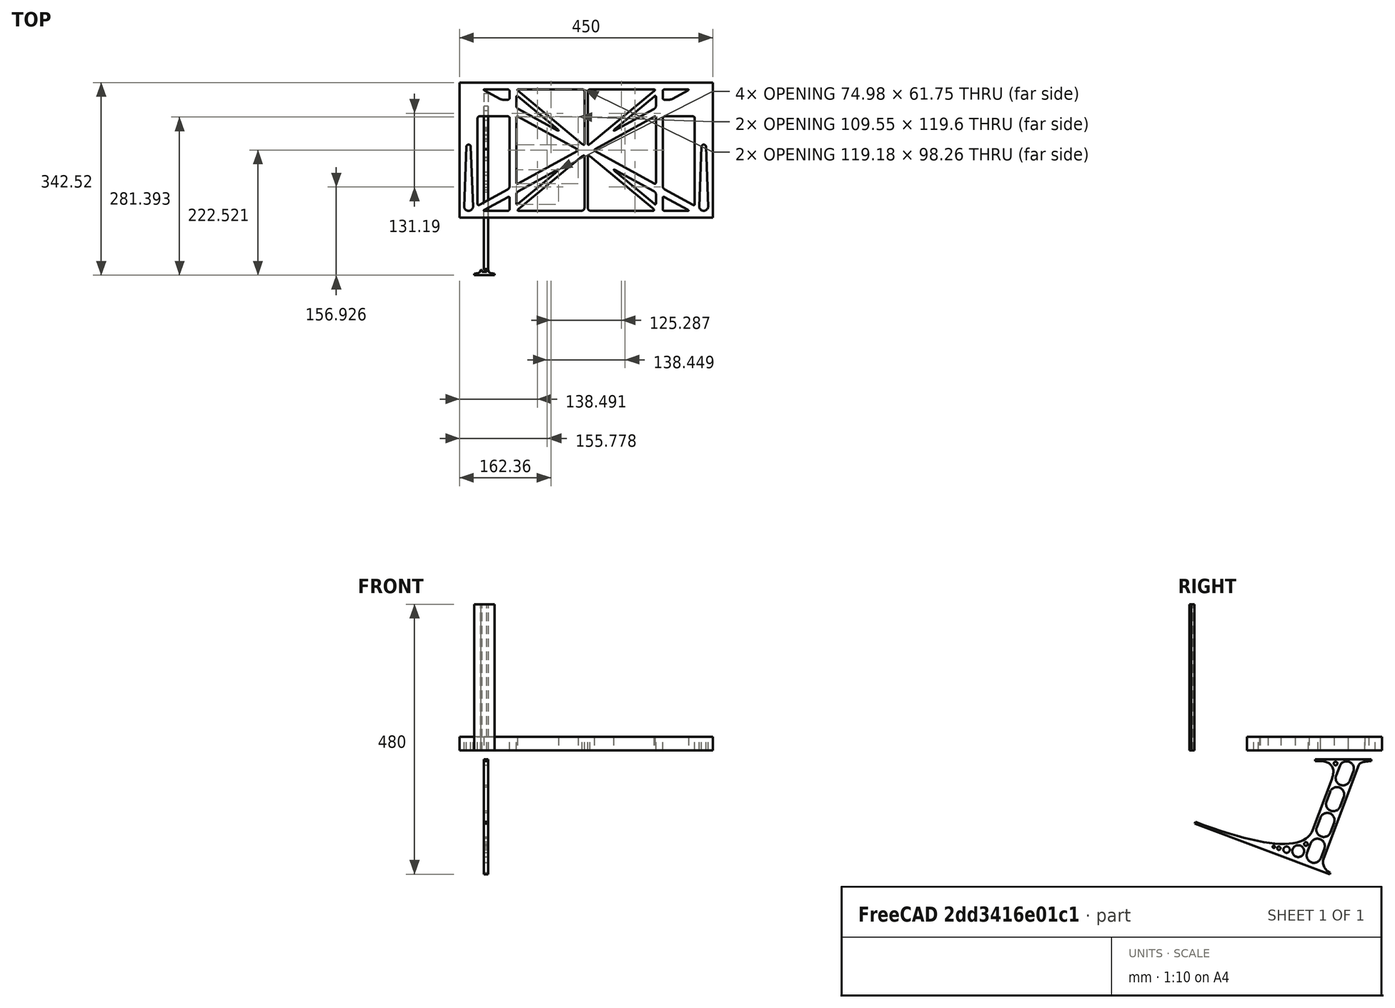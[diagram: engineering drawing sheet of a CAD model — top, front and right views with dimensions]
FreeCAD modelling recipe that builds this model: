
FCSTD DOCUMENT  (FreeCAD 0.19R0.19.2)
Label: laptopStand169FCStd
License: All rights reserved
LicenseURL: http://en.wikipedia.org/wiki/All_rights_reserved
objects: Sketcher::SketchObject×4, Part::Extrusion×3
note: 7 computed .brp shape members not serialized (recipe doc carries the construction recipe); baked Part::Feature solids carry a one-line shape summary decoded from their .brp

FEATURE [Sketcher::SketchObject] Sketch
  FullyConstrained = false
  sketch-geometry (349):
    g0: LineSegment StartX=-10.9272 StartY=-82.7794 StartZ=0 EndX=46.0728 EndY=-51.4823 EndZ=0
    g1: LineSegment StartX=-10.9272 StartY=76.4095 StartZ=0 EndX=-10.9272 EndY=-82.7794 EndZ=0
    g2: LineSegment StartX=46.0728 StartY=76.4095 StartZ=0 EndX=46.0728 EndY=-51.4823 EndZ=0
    g3: LineSegment StartX=-42.9272 StartY=136.221 StartZ=0 EndX=-42.9272 EndY=-103.779 EndZ=0
    g4: LineSegment StartX=407.073 StartY=136.221 StartZ=0 EndX=407.073 EndY=-103.779 EndZ=0
    g5: ArcOfCircle CenterX=-26.9272 CenterY=-83.7794 CenterZ=0 NormalX=0 NormalY=0 NormalZ=1 AngleXU=0 Radius=8 StartAngle=3.14159 EndAngle=6.28319
    g6: ArcOfCircle CenterX=391.073 CenterY=22.1087 CenterZ=0 NormalX=0 NormalY=0 NormalZ=1 AngleXU=0 Radius=8 StartAngle=-4.4e-15 EndAngle=3.14159
    g7: LineSegment StartX=399.073 StartY=22.1087 StartZ=0 EndX=399.073 EndY=-83.7794 EndZ=0
    g8: LineSegment StartX=383.073 StartY=22.1087 StartZ=0 EndX=383.073 EndY=-83.7794 EndZ=0
    g9: ArcOfCircle CenterX=391.073 CenterY=-83.7794 CenterZ=0 NormalX=0 NormalY=0 NormalZ=1 AngleXU=0 Radius=8 StartAngle=3.14159 EndAngle=6.28319
    g10: Circle CenterX=175.022 CenterY=27.0628 CenterZ=0 NormalX=0 NormalY=0 NormalZ=1 AngleXU=0 Radius=1
    g11: Circle CenterX=179.022 CenterY=24.8665 CenterZ=0 NormalX=0 NormalY=0 NormalZ=1 AngleXU=0 Radius=1
    g12: Circle CenterX=179.022 CenterY=27.0628 CenterZ=0 NormalX=0 NormalY=0 NormalZ=1 AngleXU=0 Radius=1
    g13: BSplineCurve PolesCount=3 KnotsCount=2 Degree=2 IsPeriodic=0
    g14: GeomPoint X=175.022 Y=27.0628 Z=0
    g15: GeomPoint X=179.022 Y=27.0628 Z=0
    g16: Circle CenterX=189.124 CenterY=27.0628 CenterZ=0 NormalX=0 NormalY=0 NormalZ=1 AngleXU=0 Radius=1
    g17: Circle CenterX=185.124 CenterY=24.8665 CenterZ=0 NormalX=0 NormalY=0 NormalZ=1 AngleXU=0 Radius=1
    g18: Circle CenterX=185.124 CenterY=27.0628 CenterZ=0 NormalX=0 NormalY=0 NormalZ=1 AngleXU=0 Radius=1
    g19: BSplineCurve PolesCount=3 KnotsCount=2 Degree=2 IsPeriodic=0
    g20: GeomPoint X=189.124 Y=27.0628 Z=0
    g21: GeomPoint X=185.124 Y=27.0628 Z=0
    g22: Circle CenterX=175.022 CenterY=5.37834 CenterZ=0 NormalX=0 NormalY=0 NormalZ=1 AngleXU=0 Radius=1
    g23: Circle CenterX=179.022 CenterY=7.57463 CenterZ=0 NormalX=0 NormalY=0 NormalZ=1 AngleXU=0 Radius=1
    g24: Circle CenterX=179.022 CenterY=5.34704 CenterZ=0 NormalX=0 NormalY=0 NormalZ=1 AngleXU=0 Radius=1
    g25: BSplineCurve PolesCount=3 KnotsCount=2 Degree=2 IsPeriodic=0
    g26: GeomPoint X=175.022 Y=5.37834 Z=0
    g27: GeomPoint X=179.022 Y=5.34704 Z=0
    g28: Circle CenterX=189.124 CenterY=5.37834 CenterZ=0 NormalX=0 NormalY=0 NormalZ=1 AngleXU=0 Radius=1
    g29: Circle CenterX=185.124 CenterY=7.57463 CenterZ=0 NormalX=0 NormalY=0 NormalZ=1 AngleXU=0 Radius=1
    g30: Circle CenterX=185.124 CenterY=5.34704 CenterZ=0 NormalX=0 NormalY=0 NormalZ=1 AngleXU=0 Radius=1
    g31: BSplineCurve PolesCount=3 KnotsCount=2 Degree=2 IsPeriodic=0
    g32: GeomPoint X=189.124 Y=5.37834 Z=0
    g33: GeomPoint X=185.124 Y=5.34704 Z=0
    g34: Circle CenterX=165.871 CenterY=18.1458 CenterZ=0 NormalX=0 NormalY=0 NormalZ=1 AngleXU=0 Radius=1
    g35: Circle CenterX=169.377 CenterY=16.2206 CenterZ=0 NormalX=0 NormalY=0 NormalZ=1 AngleXU=0 Radius=1
    g36: Circle CenterX=165.871 CenterY=14.2954 CenterZ=0 NormalX=0 NormalY=0 NormalZ=1 AngleXU=0 Radius=1
    g37: BSplineCurve PolesCount=3 KnotsCount=2 Degree=2 IsPeriodic=0
    g38: GeomPoint X=165.871 Y=18.1458 Z=0
    g39: GeomPoint X=165.871 Y=14.2954 Z=0
    g40: Circle CenterX=198.275 CenterY=18.1458 CenterZ=0 NormalX=0 NormalY=0 NormalZ=1 AngleXU=0 Radius=1
    g41: Circle CenterX=194.768 CenterY=16.2206 CenterZ=0 NormalX=0 NormalY=0 NormalZ=1 AngleXU=0 Radius=1
    g42: Circle CenterX=198.275 CenterY=14.2954 CenterZ=0 NormalX=0 NormalY=0 NormalZ=1 AngleXU=0 Radius=1
    g43: BSplineCurve PolesCount=3 KnotsCount=2 Degree=2 IsPeriodic=0
    g44: GeomPoint X=198.275 Y=18.1458 Z=0
    g45: GeomPoint X=198.275 Y=14.2954 Z=0
    g46: LineSegment StartX=407.073 StartY=-103.779 StartZ=0 EndX=-42.9272 EndY=-103.779 EndZ=0
    g47: LineSegment StartX=407.073 StartY=136.221 StartZ=0 EndX=-42.9272 EndY=136.221 EndZ=0
    g48: LineSegment StartX=46.0728 StartY=76.4095 StartZ=0 EndX=-10.9272 EndY=76.4095 EndZ=0
    g49: Circle CenterX=125.607 CenterY=54.1951 CenterZ=0 NormalX=0 NormalY=0 NormalZ=1 AngleXU=0 Radius=1
    g50: Circle CenterX=139.632 CenterY=46.4944 CenterZ=0 NormalX=0 NormalY=0 NormalZ=1 AngleXU=0 Radius=1
    g51: Circle CenterX=127.326 CenterY=56.7187 CenterZ=0 NormalX=0 NormalY=0 NormalZ=1 AngleXU=0 Radius=1
    g52: BSplineCurve PolesCount=3 KnotsCount=2 Degree=2 IsPeriodic=0
    g53: GeomPoint X=125.607 Y=54.1951 Z=0
    g54: GeomPoint X=127.326 Y=56.7187 Z=0
    g55: Circle CenterX=236.821 CenterY=56.7187 CenterZ=0 NormalX=0 NormalY=0 NormalZ=1 AngleXU=0 Radius=1
    g56: Circle CenterX=224.513 CenterY=46.4944 CenterZ=0 NormalX=0 NormalY=0 NormalZ=1 AngleXU=0 Radius=1
    g57: Circle CenterX=238.538 CenterY=54.1951 CenterZ=0 NormalX=0 NormalY=0 NormalZ=1 AngleXU=0 Radius=1
    g58: BSplineCurve PolesCount=3 KnotsCount=2 Degree=2 IsPeriodic=0
    g59: GeomPoint X=236.821 Y=56.7187 Z=0
    g60: GeomPoint X=238.538 Y=54.1951 Z=0
    g61: Circle CenterX=238.538 CenterY=-21.7539 CenterZ=0 NormalX=0 NormalY=0 NormalZ=1 AngleXU=0 Radius=1
    g62: Circle CenterX=224.513 CenterY=-14.0532 CenterZ=0 NormalX=0 NormalY=0 NormalZ=1 AngleXU=0 Radius=1
    g63: Circle CenterX=236.821 CenterY=-24.2775 CenterZ=0 NormalX=0 NormalY=0 NormalZ=1 AngleXU=0 Radius=1
    g64: BSplineCurve PolesCount=3 KnotsCount=2 Degree=2 IsPeriodic=0
    g65: GeomPoint X=238.538 Y=-21.7539 Z=0
    g66: GeomPoint X=236.821 Y=-24.2775 Z=0
    g67: Circle CenterX=125.607 CenterY=-21.7539 CenterZ=0 NormalX=0 NormalY=0 NormalZ=1 AngleXU=0 Radius=1
    g68: Circle CenterX=139.632 CenterY=-14.0532 CenterZ=0 NormalX=0 NormalY=0 NormalZ=1 AngleXU=0 Radius=1
    g69: Circle CenterX=127.325 CenterY=-24.2775 CenterZ=0 NormalX=0 NormalY=0 NormalZ=1 AngleXU=0 Radius=1
    g70: BSplineCurve PolesCount=3 KnotsCount=2 Degree=2 IsPeriodic=0
    g71: GeomPoint X=125.607 Y=-21.7539 Z=0
    g72: GeomPoint X=127.325 Y=-24.2775 Z=0
    g73: Circle CenterX=302.996 CenterY=111.695 CenterZ=0 NormalX=0 NormalY=0 NormalZ=1 AngleXU=0 Radius=1
    g74: Circle CenterX=306.073 CenterY=114.251 CenterZ=0 NormalX=0 NormalY=0 NormalZ=1 AngleXU=0 Radius=1
    g75: Circle CenterX=306.073 CenterY=110.251 CenterZ=0 NormalX=0 NormalY=0 NormalZ=1 AngleXU=0 Radius=1
    g76: BSplineCurve PolesCount=3 KnotsCount=2 Degree=2 IsPeriodic=0
    g77: GeomPoint X=302.996 Y=111.695 Z=0
    g78: GeomPoint X=306.073 Y=110.251 Z=0
    g79: Circle CenterX=306.073 CenterY=95.2763 CenterZ=0 NormalX=0 NormalY=0 NormalZ=1 AngleXU=0 Radius=1
    g80: Circle CenterX=306.073 CenterY=91.2763 CenterZ=0 NormalX=0 NormalY=0 NormalZ=1 AngleXU=0 Radius=1
    g81: Circle CenterX=302.567 CenterY=89.3511 CenterZ=0 NormalX=0 NormalY=0 NormalZ=1 AngleXU=0 Radius=1
    g82: BSplineCurve PolesCount=3 KnotsCount=2 Degree=2 IsPeriodic=0
    g83: GeomPoint X=306.073 Y=95.2763 Z=0
    g84: GeomPoint X=302.567 Y=89.3511 Z=0
    g85: LineSegment StartX=306.073 StartY=110.251 StartZ=0 EndX=306.073 EndY=95.2763 EndZ=0
    g86: LineSegment StartX=302.996 StartY=111.695 StartZ=0 EndX=236.821 EndY=56.7187 EndZ=0
    g87: LineSegment StartX=238.538 StartY=54.1951 StartZ=0 EndX=302.567 EndY=89.3511 EndZ=0
    g88: Circle CenterX=61.1496 CenterY=111.695 CenterZ=0 NormalX=0 NormalY=0 NormalZ=1 AngleXU=0 Radius=1
    g89: Circle CenterX=58.0728 CenterY=114.251 CenterZ=0 NormalX=0 NormalY=0 NormalZ=1 AngleXU=0 Radius=1
    g90: Circle CenterX=58.0728 CenterY=110.251 CenterZ=0 NormalX=0 NormalY=0 NormalZ=1 AngleXU=0 Radius=1
    g91: BSplineCurve PolesCount=3 KnotsCount=2 Degree=2 IsPeriodic=0
    g92: GeomPoint X=61.1496 Y=111.695 Z=0
    g93: GeomPoint X=58.0728 Y=110.251 Z=0
    g94: Circle CenterX=61.5791 CenterY=89.3511 CenterZ=0 NormalX=0 NormalY=0 NormalZ=1 AngleXU=0 Radius=1
    g95: Circle CenterX=58.0728 CenterY=91.2763 CenterZ=0 NormalX=0 NormalY=0 NormalZ=1 AngleXU=0 Radius=1
    g96: Circle CenterX=58.0728 CenterY=95.2763 CenterZ=0 NormalX=0 NormalY=0 NormalZ=1 AngleXU=0 Radius=1
    g97: BSplineCurve PolesCount=3 KnotsCount=2 Degree=2 IsPeriodic=0
    g98: GeomPoint X=61.5791 Y=89.3511 Z=0
    g99: GeomPoint X=58.0728 Y=95.2763 Z=0
    g100: LineSegment StartX=58.0728 StartY=110.251 StartZ=0 EndX=58.0728 EndY=95.2763 EndZ=0
    g101: LineSegment StartX=61.1496 StartY=111.695 StartZ=0 EndX=127.326 EndY=56.7187 EndZ=0
    g102: LineSegment StartX=125.607 StartY=54.1951 StartZ=0 EndX=61.5791 EndY=89.3511 EndZ=0
    g103: Circle CenterX=61.5791 CenterY=-56.9099 CenterZ=0 NormalX=0 NormalY=0 NormalZ=1 AngleXU=0 Radius=1
    g104: Circle CenterX=58.0728 CenterY=-58.8351 CenterZ=0 NormalX=0 NormalY=0 NormalZ=1 AngleXU=0 Radius=1
    g105: Circle CenterX=58.0728 CenterY=-62.8351 CenterZ=0 NormalX=0 NormalY=0 NormalZ=1 AngleXU=0 Radius=1
    g106: BSplineCurve PolesCount=3 KnotsCount=2 Degree=2 IsPeriodic=0
    g107: GeomPoint X=61.5791 Y=-56.9099 Z=0
    g108: GeomPoint X=58.0728 Y=-62.8351 Z=0
    g109: Circle CenterX=58.0728 CenterY=-77.8102 CenterZ=0 NormalX=0 NormalY=0 NormalZ=1 AngleXU=0 Radius=1
    g110: Circle CenterX=58.0728 CenterY=-81.8102 CenterZ=0 NormalX=0 NormalY=0 NormalZ=1 AngleXU=0 Radius=1
    g111: Circle CenterX=61.1496 CenterY=-79.2541 CenterZ=0 NormalX=0 NormalY=0 NormalZ=1 AngleXU=0 Radius=1
    g112: BSplineCurve PolesCount=3 KnotsCount=2 Degree=2 IsPeriodic=0
    g113: GeomPoint X=58.0728 Y=-77.8102 Z=0
    g114: GeomPoint X=61.1496 Y=-79.2541 Z=0
    g115: LineSegment StartX=58.0728 StartY=-62.8351 StartZ=0 EndX=58.0728 EndY=-77.8102 EndZ=0
    g116: LineSegment StartX=61.1496 StartY=-79.2541 StartZ=0 EndX=127.325 EndY=-24.2775 EndZ=0
    g117: LineSegment StartX=125.607 StartY=-21.7539 StartZ=0 EndX=61.5791 EndY=-56.9099 EndZ=0
    g118: Circle CenterX=302.567 CenterY=-56.9099 CenterZ=0 NormalX=0 NormalY=0 NormalZ=1 AngleXU=0 Radius=1
    g119: Circle CenterX=306.073 CenterY=-58.8351 CenterZ=0 NormalX=0 NormalY=0 NormalZ=1 AngleXU=0 Radius=1
    g120: Circle CenterX=306.073 CenterY=-62.8351 CenterZ=0 NormalX=0 NormalY=0 NormalZ=1 AngleXU=0 Radius=1
    g121: BSplineCurve PolesCount=3 KnotsCount=2 Degree=2 IsPeriodic=0
    g122: GeomPoint X=302.567 Y=-56.9099 Z=0
    g123: GeomPoint X=306.073 Y=-62.8351 Z=0
    g124: Circle CenterX=302.996 CenterY=-79.2541 CenterZ=0 NormalX=0 NormalY=0 NormalZ=1 AngleXU=0 Radius=1
    g125: Circle CenterX=306.073 CenterY=-81.8102 CenterZ=0 NormalX=0 NormalY=0 NormalZ=1 AngleXU=0 Radius=1
    g126: Circle CenterX=306.073 CenterY=-77.8102 CenterZ=0 NormalX=0 NormalY=0 NormalZ=1 AngleXU=0 Radius=1
    g127: BSplineCurve PolesCount=3 KnotsCount=2 Degree=2 IsPeriodic=0
    g128: GeomPoint X=302.996 Y=-79.2541 Z=0
    g129: GeomPoint X=306.073 Y=-77.8102 Z=0
    g130: LineSegment StartX=306.073 StartY=-62.8351 StartZ=0 EndX=306.073 EndY=-77.8102 EndZ=0
    g131: LineSegment StartX=302.996 StartY=-79.2541 StartZ=0 EndX=236.821 EndY=-24.2775 EndZ=0
    g132: LineSegment StartX=238.538 StartY=-21.7539 StartZ=0 EndX=302.567 EndY=-56.9099 EndZ=0
    g133: Circle CenterX=61.6457 CenterY=-88.8112 CenterZ=0 NormalX=0 NormalY=0 NormalZ=1 AngleXU=0 Radius=1
    g134: Circle CenterX=58.0728 CenterY=-91.7794 CenterZ=0 NormalX=0 NormalY=0 NormalZ=1 AngleXU=0 Radius=1
    g135: Circle CenterX=63.9135 CenterY=-91.7794 CenterZ=0 NormalX=0 NormalY=0 NormalZ=1 AngleXU=0 Radius=1
    g136: BSplineCurve PolesCount=3 KnotsCount=2 Degree=2 IsPeriodic=0
    g137: GeomPoint X=61.6457 Y=-88.8112 Z=0
    g138: GeomPoint X=63.9135 Y=-91.7794 Z=0
    g139: Circle CenterX=179.022 CenterY=-85.8163 CenterZ=0 NormalX=0 NormalY=0 NormalZ=1 AngleXU=0 Radius=1
    g140: Circle CenterX=179.022 CenterY=-91.7794 CenterZ=0 NormalX=0 NormalY=0 NormalZ=1 AngleXU=0 Radius=1
    g141: Circle CenterX=171.895 CenterY=-91.7794 CenterZ=0 NormalX=0 NormalY=0 NormalZ=1 AngleXU=0 Radius=1
    g142: BSplineCurve PolesCount=3 KnotsCount=2 Degree=2 IsPeriodic=0
    g143: GeomPoint X=179.022 Y=-85.8163 Z=0
    g144: GeomPoint X=171.895 Y=-91.7794 Z=0
    g145: Circle CenterX=185.124 CenterY=-86.2028 CenterZ=0 NormalX=0 NormalY=0 NormalZ=1 AngleXU=0 Radius=1
    g146: Circle CenterX=185.124 CenterY=-91.7794 CenterZ=0 NormalX=0 NormalY=0 NormalZ=1 AngleXU=0 Radius=1
    g147: Circle CenterX=191.747 CenterY=-91.7794 CenterZ=0 NormalX=0 NormalY=0 NormalZ=1 AngleXU=0 Radius=1
    g148: BSplineCurve PolesCount=3 KnotsCount=2 Degree=2 IsPeriodic=0
    g149: GeomPoint X=185.124 Y=-86.2028 Z=0
    g150: GeomPoint X=191.747 Y=-91.7794 Z=0
    g151: Circle CenterX=299.888 CenterY=-86.6413 CenterZ=0 NormalX=0 NormalY=0 NormalZ=1 AngleXU=0 Radius=1
    g152: Circle CenterX=306.073 CenterY=-91.7794 CenterZ=0 NormalX=0 NormalY=0 NormalZ=1 AngleXU=0 Radius=1
    g153: Circle CenterX=298.776 CenterY=-91.7794 CenterZ=0 NormalX=0 NormalY=0 NormalZ=1 AngleXU=0 Radius=1
    g154: BSplineCurve PolesCount=3 KnotsCount=2 Degree=2 IsPeriodic=0
    g155: GeomPoint X=299.888 Y=-86.6413 Z=0
    g156: GeomPoint X=298.776 Y=-91.7794 Z=0
    g157: LineSegment StartX=189.124 StartY=5.37834 StartZ=0 EndX=299.888 EndY=-86.6413 EndZ=0
    g158: LineSegment StartX=298.776 StartY=-91.7794 StartZ=0 EndX=191.747 EndY=-91.7794 EndZ=0
    g159: LineSegment StartX=185.124 StartY=-86.2028 StartZ=0 EndX=185.124 EndY=5.34704 EndZ=0
    g160: LineSegment StartX=179.022 StartY=5.34704 StartZ=0 EndX=179.022 EndY=-85.8163 EndZ=0
    g161: LineSegment StartX=171.895 StartY=-91.7794 StartZ=0 EndX=63.9135 EndY=-91.7794 EndZ=0
    g162: LineSegment StartX=61.6457 StartY=-88.8112 StartZ=0 EndX=175.022 EndY=5.37834 EndZ=0
    g163: Circle CenterX=302.073 CenterY=124.221 CenterZ=0 NormalX=0 NormalY=0 NormalZ=1 AngleXU=0 Radius=1
    g164: Circle CenterX=306.073 CenterY=124.221 CenterZ=0 NormalX=0 NormalY=0 NormalZ=1 AngleXU=0 Radius=1
    g165: Circle CenterX=302.996 CenterY=121.665 CenterZ=0 NormalX=0 NormalY=0 NormalZ=1 AngleXU=0 Radius=1
    g166: BSplineCurve PolesCount=3 KnotsCount=2 Degree=2 IsPeriodic=0
    g167: GeomPoint X=302.073 Y=124.221 Z=0
    g168: GeomPoint X=302.996 Y=121.665 Z=0
    g169: Circle CenterX=189.124 CenterY=124.221 CenterZ=0 NormalX=0 NormalY=0 NormalZ=1 AngleXU=0 Radius=1
    g170: Circle CenterX=185.124 CenterY=124.221 CenterZ=0 NormalX=0 NormalY=0 NormalZ=1 AngleXU=0 Radius=1
    g171: Circle CenterX=185.124 CenterY=120.221 CenterZ=0 NormalX=0 NormalY=0 NormalZ=1 AngleXU=0 Radius=1
    g172: BSplineCurve PolesCount=3 KnotsCount=2 Degree=2 IsPeriodic=0
    g173: GeomPoint X=189.124 Y=124.221 Z=0
    g174: GeomPoint X=185.124 Y=120.221 Z=0
    g175: Circle CenterX=175.022 CenterY=124.221 CenterZ=0 NormalX=0 NormalY=0 NormalZ=1 AngleXU=0 Radius=1
    g176: Circle CenterX=179.022 CenterY=124.221 CenterZ=0 NormalX=0 NormalY=0 NormalZ=1 AngleXU=0 Radius=1
    g177: Circle CenterX=179.022 CenterY=120.221 CenterZ=0 NormalX=0 NormalY=0 NormalZ=1 AngleXU=0 Radius=1
    g178: BSplineCurve PolesCount=3 KnotsCount=2 Degree=2 IsPeriodic=0
    g179: GeomPoint X=175.022 Y=124.221 Z=0
    g180: GeomPoint X=179.022 Y=120.221 Z=0
    g181: Circle CenterX=62.0728 CenterY=124.221 CenterZ=0 NormalX=0 NormalY=0 NormalZ=1 AngleXU=0 Radius=1
    g182: Circle CenterX=58.0728 CenterY=124.221 CenterZ=0 NormalX=0 NormalY=0 NormalZ=1 AngleXU=0 Radius=1
    g183: Circle CenterX=61.1496 CenterY=121.665 CenterZ=0 NormalX=0 NormalY=0 NormalZ=1 AngleXU=0 Radius=1
    g184: BSplineCurve PolesCount=3 KnotsCount=2 Degree=2 IsPeriodic=0
    g185: GeomPoint X=62.0728 Y=124.221 Z=0
    g186: GeomPoint X=61.1496 Y=121.665 Z=0
    g187: LineSegment StartX=62.0728 StartY=124.221 StartZ=0 EndX=175.022 EndY=124.221 EndZ=0
    g188: LineSegment StartX=179.022 StartY=120.221 StartZ=0 EndX=179.022 EndY=27.0628 EndZ=0
    g189: LineSegment StartX=185.124 StartY=27.0628 StartZ=0 EndX=185.124 EndY=120.221 EndZ=0
    g190: LineSegment StartX=189.124 StartY=124.221 StartZ=0 EndX=302.073 EndY=124.221 EndZ=0
    g191: LineSegment StartX=302.996 StartY=121.665 StartZ=0 EndX=189.124 EndY=27.0628 EndZ=0
    g192: LineSegment StartX=175.022 StartY=27.0628 StartZ=0 EndX=61.1496 EndY=121.665 EndZ=0
    g193: Circle CenterX=61.5791 CenterY=75.4095 CenterZ=0 NormalX=0 NormalY=0 NormalZ=1 AngleXU=0 Radius=1
    g194: Circle CenterX=58.0728 CenterY=77.3346 CenterZ=0 NormalX=0 NormalY=0 NormalZ=1 AngleXU=0 Radius=1
    g195: Circle CenterX=58.0728 CenterY=73.3346 CenterZ=0 NormalX=0 NormalY=0 NormalZ=1 AngleXU=0 Radius=1
    g196: BSplineCurve PolesCount=3 KnotsCount=2 Degree=2 IsPeriodic=0
    g197: GeomPoint X=61.5791 Y=75.4095 Z=0
    g198: GeomPoint X=58.0728 Y=73.3346 Z=0
    g199: Circle CenterX=58.0728 CenterY=-40.8935 CenterZ=0 NormalX=0 NormalY=0 NormalZ=1 AngleXU=0 Radius=1
    g200: Circle CenterX=58.0728 CenterY=-44.8935 CenterZ=0 NormalX=0 NormalY=0 NormalZ=1 AngleXU=0 Radius=1
    g201: Circle CenterX=61.5791 CenterY=-42.9683 CenterZ=0 NormalX=0 NormalY=0 NormalZ=1 AngleXU=0 Radius=1
    g202: BSplineCurve PolesCount=3 KnotsCount=2 Degree=2 IsPeriodic=0
    g203: GeomPoint X=58.0728 Y=-40.8935 Z=0
    g204: GeomPoint X=61.5791 Y=-42.9683 Z=0
    g205: LineSegment StartX=61.5791 StartY=-42.9683 StartZ=0 EndX=165.871 EndY=14.2954 EndZ=0
    g206: LineSegment StartX=165.871 StartY=18.1458 StartZ=0 EndX=61.5791 EndY=75.4095 EndZ=0
    g207: LineSegment StartX=58.0728 StartY=73.3346 StartZ=0 EndX=58.0728 EndY=-40.8935 EndZ=0
    g208: Circle CenterX=302.567 CenterY=-42.9683 CenterZ=0 NormalX=0 NormalY=0 NormalZ=1 AngleXU=0 Radius=1
    g209: Circle CenterX=306.073 CenterY=-44.8935 CenterZ=0 NormalX=0 NormalY=0 NormalZ=1 AngleXU=0 Radius=1
    g210: Circle CenterX=306.073 CenterY=-40.8935 CenterZ=0 NormalX=0 NormalY=0 NormalZ=1 AngleXU=0 Radius=1
    g211: BSplineCurve PolesCount=3 KnotsCount=2 Degree=2 IsPeriodic=0
    g212: GeomPoint X=302.567 Y=-42.9683 Z=0
    g213: GeomPoint X=306.073 Y=-40.8935 Z=0
    g214: Circle CenterX=306.073 CenterY=73.3346 CenterZ=0 NormalX=0 NormalY=0 NormalZ=1 AngleXU=0 Radius=1
    g215: Circle CenterX=306.073 CenterY=77.3346 CenterZ=0 NormalX=0 NormalY=0 NormalZ=1 AngleXU=0 Radius=1
    g216: Circle CenterX=302.567 CenterY=75.4095 CenterZ=0 NormalX=0 NormalY=0 NormalZ=1 AngleXU=0 Radius=1
    g217: BSplineCurve PolesCount=3 KnotsCount=2 Degree=2 IsPeriodic=0
    g218: GeomPoint X=306.073 Y=73.3346 Z=0
    g219: GeomPoint X=302.567 Y=75.4095 Z=0
    g220: LineSegment StartX=302.567 StartY=-42.9683 StartZ=0 EndX=198.275 EndY=14.2954 EndZ=0
    g221: LineSegment StartX=198.275 StartY=18.1458 StartZ=0 EndX=302.567 EndY=75.4095 EndZ=0
    g222: LineSegment StartX=306.073 StartY=73.3346 StartZ=0 EndX=306.073 EndY=-40.8935 EndZ=0
    g223: LineSegment StartX=322.073 StartY=105.865 StartZ=0 EndX=328.643 EndY=105.865 EndZ=0
    g224: LineSegment StartX=318.073 StartY=120.221 StartZ=0 EndX=318.073 EndY=109.865 EndZ=0
    g225: LineSegment StartX=336.157 StartY=107.779 StartZ=0 EndX=362.567 EndY=122.294 EndZ=0
    g226: Circle CenterX=362.073 CenterY=124.221 CenterZ=0 NormalX=0 NormalY=0 NormalZ=1 AngleXU=0 Radius=1
    g227: Circle CenterX=366.073 CenterY=124.221 CenterZ=0 NormalX=0 NormalY=0 NormalZ=1 AngleXU=0 Radius=1
    g228: Circle CenterX=362.567 CenterY=122.294 CenterZ=0 NormalX=0 NormalY=0 NormalZ=1 AngleXU=0 Radius=1
    g229: BSplineCurve PolesCount=3 KnotsCount=2 Degree=2 IsPeriodic=0
    g230: GeomPoint X=362.073 Y=124.221 Z=0
    g231: GeomPoint X=362.567 Y=122.294 Z=0
    g232: Circle CenterX=322.073 CenterY=124.221 CenterZ=0 NormalX=0 NormalY=0 NormalZ=1 AngleXU=0 Radius=1
    g233: Circle CenterX=318.073 CenterY=124.221 CenterZ=0 NormalX=0 NormalY=0 NormalZ=1 AngleXU=0 Radius=1
    g234: Circle CenterX=318.073 CenterY=120.221 CenterZ=0 NormalX=0 NormalY=0 NormalZ=1 AngleXU=0 Radius=1
    g235: BSplineCurve PolesCount=3 KnotsCount=2 Degree=2 IsPeriodic=0
    g236: GeomPoint X=322.073 Y=124.221 Z=0
    g237: GeomPoint X=318.073 Y=120.221 Z=0
    g238: Circle CenterX=322.073 CenterY=105.865 CenterZ=0 NormalX=0 NormalY=0 NormalZ=1 AngleXU=0 Radius=1
    g239: Circle CenterX=318.073 CenterY=105.865 CenterZ=0 NormalX=0 NormalY=0 NormalZ=1 AngleXU=0 Radius=1
    g240: Circle CenterX=318.073 CenterY=109.865 CenterZ=0 NormalX=0 NormalY=0 NormalZ=1 AngleXU=0 Radius=1
    g241: BSplineCurve PolesCount=3 KnotsCount=2 Degree=2 IsPeriodic=0
    g242: GeomPoint X=322.073 Y=105.865 Z=0
    g243: GeomPoint X=318.073 Y=109.865 Z=0
    g244: Circle CenterX=336.157 CenterY=107.779 CenterZ=0 NormalX=0 NormalY=0 NormalZ=1 AngleXU=0 Radius=1
    g245: Circle CenterX=332.651 CenterY=105.853 CenterZ=0 NormalX=0 NormalY=0 NormalZ=1 AngleXU=0 Radius=1
    g246: Circle CenterX=328.643 CenterY=105.865 CenterZ=0 NormalX=0 NormalY=0 NormalZ=1 AngleXU=0 Radius=1
    g247: BSplineCurve PolesCount=3 KnotsCount=2 Degree=2 IsPeriodic=0
    g248: GeomPoint X=336.157 Y=107.779 Z=0
    g249: GeomPoint X=328.643 Y=105.865 Z=0
    g250: LineSegment StartX=322.073 StartY=124.221 StartZ=0 EndX=362.073 EndY=124.221 EndZ=0
    g251: Circle CenterX=371.567 CenterY=-80.8644 CenterZ=0 NormalX=0 NormalY=0 NormalZ=1 AngleXU=0 Radius=1
    g252: Circle CenterX=375.073 CenterY=-82.7896 CenterZ=0 NormalX=0 NormalY=0 NormalZ=1 AngleXU=0 Radius=1
    g253: Circle CenterX=375.073 CenterY=-78.7896 CenterZ=0 NormalX=0 NormalY=0 NormalZ=1 AngleXU=0 Radius=1
    g254: BSplineCurve PolesCount=3 KnotsCount=2 Degree=2 IsPeriodic=0
    g255: GeomPoint X=371.567 Y=-80.8644 Z=0
    g256: GeomPoint X=375.073 Y=-78.7896 Z=0
    g257: Circle CenterX=321.579 CenterY=-53.4075 CenterZ=0 NormalX=0 NormalY=0 NormalZ=1 AngleXU=0 Radius=1
    g258: Circle CenterX=318.073 CenterY=-51.4823 CenterZ=0 NormalX=0 NormalY=0 NormalZ=1 AngleXU=0 Radius=1
    g259: Circle CenterX=318.073 CenterY=-47.4805 CenterZ=0 NormalX=0 NormalY=0 NormalZ=1 AngleXU=0 Radius=1
    g260: BSplineCurve PolesCount=3 KnotsCount=2 Degree=2 IsPeriodic=0
    g261: GeomPoint X=321.579 Y=-53.4075 Z=0
    g262: GeomPoint X=318.073 Y=-47.4805 Z=0
    g263: LineSegment StartX=371.567 StartY=-80.8644 StartZ=0 EndX=321.579 EndY=-53.4075 EndZ=0
    g264: Circle CenterX=321.579 CenterY=-67.3492 CenterZ=0 NormalX=0 NormalY=0 NormalZ=1 AngleXU=0 Radius=1
    g265: Circle CenterX=318.073 CenterY=-65.424 CenterZ=0 NormalX=0 NormalY=0 NormalZ=1 AngleXU=0 Radius=1
    g266: Circle CenterX=318.073 CenterY=-69.424 CenterZ=0 NormalX=0 NormalY=0 NormalZ=1 AngleXU=0 Radius=1
    g267: BSplineCurve PolesCount=3 KnotsCount=2 Degree=2 IsPeriodic=0
    g268: GeomPoint X=321.579 Y=-67.3492 Z=0
    g269: GeomPoint X=318.073 Y=-69.424 Z=0
    g270: Circle CenterX=362.567 CenterY=-89.8542 CenterZ=0 NormalX=0 NormalY=0 NormalZ=1 AngleXU=0 Radius=1
    g271: Circle CenterX=366.073 CenterY=-91.7794 CenterZ=0 NormalX=0 NormalY=0 NormalZ=1 AngleXU=0 Radius=1
    g272: Circle CenterX=362.073 CenterY=-91.7794 CenterZ=0 NormalX=0 NormalY=0 NormalZ=1 AngleXU=0 Radius=1
    g273: BSplineCurve PolesCount=3 KnotsCount=2 Degree=2 IsPeriodic=0
    g274: GeomPoint X=362.567 Y=-89.8542 Z=0
    g275: GeomPoint X=362.073 Y=-91.7794 Z=0
    g276: Circle CenterX=322.073 CenterY=-91.7794 CenterZ=0 NormalX=0 NormalY=0 NormalZ=1 AngleXU=0 Radius=1
    g277: Circle CenterX=318.073 CenterY=-91.7794 CenterZ=0 NormalX=0 NormalY=0 NormalZ=1 AngleXU=0 Radius=1
    g278: Circle CenterX=318.073 CenterY=-87.7794 CenterZ=0 NormalX=0 NormalY=0 NormalZ=1 AngleXU=0 Radius=1
    g279: BSplineCurve PolesCount=3 KnotsCount=2 Degree=2 IsPeriodic=0
    g280: GeomPoint X=322.073 Y=-91.7794 Z=0
    g281: GeomPoint X=318.073 Y=-87.7794 Z=0
    g282: LineSegment StartX=362.567 StartY=-89.8542 StartZ=0 EndX=321.579 EndY=-67.3492 EndZ=0
    g283: LineSegment StartX=318.073 StartY=-69.424 StartZ=0 EndX=318.073 EndY=-87.7794 EndZ=0
    g284: LineSegment StartX=322.073 StartY=-91.7794 StartZ=0 EndX=362.073 EndY=-91.7794 EndZ=0
    g285: Circle CenterX=2.07281 CenterY=124.221 CenterZ=0 NormalX=0 NormalY=0 NormalZ=1 AngleXU=0 Radius=1
    g286: Circle CenterX=1.57905 CenterY=122.295 CenterZ=0 NormalX=0 NormalY=0 NormalZ=1 AngleXU=0 Radius=1
    g287: BSplineCurve PolesCount=3 KnotsCount=2 Degree=2 IsPeriodic=0
    g288: GeomPoint X=2.07281 Y=124.221 Z=0
    g289: GeomPoint X=1.57905 Y=122.295 Z=0
    g290: Circle CenterX=42.0728 CenterY=124.221 CenterZ=0 NormalX=0 NormalY=0 NormalZ=1 AngleXU=0 Radius=1
    g291: Circle CenterX=46.0728 CenterY=124.221 CenterZ=0 NormalX=0 NormalY=0 NormalZ=1 AngleXU=0 Radius=1
    g292: Circle CenterX=46.0728 CenterY=120.221 CenterZ=0 NormalX=0 NormalY=0 NormalZ=1 AngleXU=0 Radius=1
    g293: BSplineCurve PolesCount=3 KnotsCount=2 Degree=2 IsPeriodic=0
    g294: GeomPoint X=42.0728 Y=124.221 Z=0
    g295: GeomPoint X=46.0728 Y=120.221 Z=0
    g296: Circle CenterX=46.0728 CenterY=109.865 CenterZ=0 NormalX=0 NormalY=0 NormalZ=1 AngleXU=0 Radius=1
    g297: Circle CenterX=46.0728 CenterY=105.865 CenterZ=0 NormalX=0 NormalY=0 NormalZ=1 AngleXU=0 Radius=1
    g298: Circle CenterX=42.0728 CenterY=105.865 CenterZ=0 NormalX=0 NormalY=0 NormalZ=1 AngleXU=0 Radius=1
    g299: BSplineCurve PolesCount=3 KnotsCount=2 Degree=2 IsPeriodic=0
    g300: GeomPoint X=46.0728 Y=109.865 Z=0
    g301: GeomPoint X=42.0728 Y=105.865 Z=0
    g302: Circle CenterX=35.5028 CenterY=105.865 CenterZ=0 NormalX=0 NormalY=0 NormalZ=1 AngleXU=0 Radius=1
    g303: Circle CenterX=31.5028 CenterY=105.865 CenterZ=0 NormalX=0 NormalY=0 NormalZ=1 AngleXU=0 Radius=1
    g304: Circle CenterX=27.9965 CenterY=107.79 CenterZ=0 NormalX=0 NormalY=0 NormalZ=1 AngleXU=0 Radius=1
    g305: BSplineCurve PolesCount=3 KnotsCount=2 Degree=2 IsPeriodic=0
    g306: GeomPoint X=35.5028 Y=105.865 Z=0
    g307: GeomPoint X=27.9965 Y=107.79 Z=0
    g308: LineSegment StartX=2.07281 StartY=124.221 StartZ=0 EndX=42.0728 EndY=124.221 EndZ=0
    g309: LineSegment StartX=46.0728 StartY=120.221 StartZ=0 EndX=46.0728 EndY=109.865 EndZ=0
    g310: LineSegment StartX=42.0728 StartY=105.865 StartZ=0 EndX=35.5028 EndY=105.865 EndZ=0
    g311: LineSegment StartX=27.9965 StartY=107.79 StartZ=0 EndX=1.57905 EndY=122.295 EndZ=0
    g312: Circle CenterX=42.5666 CenterY=-67.3492 CenterZ=0 NormalX=0 NormalY=0 NormalZ=1 AngleXU=0 Radius=1
    g313: Circle CenterX=46.0728 CenterY=-65.424 CenterZ=0 NormalX=0 NormalY=0 NormalZ=1 AngleXU=0 Radius=1
    g314: Circle CenterX=46.0728 CenterY=-69.424 CenterZ=0 NormalX=0 NormalY=0 NormalZ=1 AngleXU=0 Radius=1
    g315: BSplineCurve PolesCount=3 KnotsCount=2 Degree=2 IsPeriodic=0
    g316: GeomPoint X=42.5666 Y=-67.3492 Z=0
    g317: GeomPoint X=46.0728 Y=-69.424 Z=0
    g318: Circle CenterX=46.0728 CenterY=-87.7794 CenterZ=0 NormalX=0 NormalY=0 NormalZ=1 AngleXU=0 Radius=1
    g319: Circle CenterX=46.0728 CenterY=-91.7794 CenterZ=0 NormalX=0 NormalY=0 NormalZ=1 AngleXU=0 Radius=1
    g320: Circle CenterX=42.0728 CenterY=-91.7794 CenterZ=0 NormalX=0 NormalY=0 NormalZ=1 AngleXU=0 Radius=1
    g321: BSplineCurve PolesCount=3 KnotsCount=2 Degree=2 IsPeriodic=0
    g322: GeomPoint X=46.0728 Y=-87.7794 Z=0
    g323: GeomPoint X=42.0728 Y=-91.7794 Z=0
    g324: Circle CenterX=2.07281 CenterY=-91.7794 CenterZ=0 NormalX=0 NormalY=0 NormalZ=1 AngleXU=0 Radius=1
    g325: Circle CenterX=-1.92719 CenterY=-91.7794 CenterZ=0 NormalX=0 NormalY=0 NormalZ=1 AngleXU=0 Radius=1
    g326: Circle CenterX=1.57905 CenterY=-89.8542 CenterZ=0 NormalX=0 NormalY=0 NormalZ=1 AngleXU=0 Radius=1
    g327: BSplineCurve PolesCount=3 KnotsCount=2 Degree=2 IsPeriodic=0
    g328: GeomPoint X=2.07281 Y=-91.7794 Z=0
    g329: GeomPoint X=1.57905 Y=-89.8542 Z=0
    g330: LineSegment StartX=2.07281 StartY=-91.7794 StartZ=0 EndX=42.0728 EndY=-91.7794 EndZ=0
    g331: LineSegment StartX=46.0728 StartY=-87.7794 StartZ=0 EndX=46.0728 EndY=-69.424 EndZ=0
    g332: LineSegment StartX=42.5666 StartY=-67.3492 StartZ=0 EndX=1.57905 EndY=-89.8542 EndZ=0
    g333: Circle CenterX=322.073 CenterY=76.4095 CenterZ=0 NormalX=0 NormalY=0 NormalZ=1 AngleXU=0 Radius=4
    g334: BSplineCurve PolesCount=3 KnotsCount=2 Degree=2 IsPeriodic=0
    g335: GeomPoint X=318.073 Y=72.4095 Z=0
    g336: GeomPoint X=322.073 Y=76.4095 Z=0
    g337: Circle CenterX=375.073 CenterY=72.4095 CenterZ=0 NormalX=0 NormalY=0 NormalZ=1 AngleXU=0 Radius=1
    g338: Circle CenterX=375.073 CenterY=76.4095 CenterZ=0 NormalX=0 NormalY=0 NormalZ=1 AngleXU=0 Radius=1
    g339: Circle CenterX=371.073 CenterY=76.4095 CenterZ=0 NormalX=0 NormalY=0 NormalZ=1 AngleXU=0 Radius=1
    g340: BSplineCurve PolesCount=3 KnotsCount=2 Degree=2 IsPeriodic=0
    g341: GeomPoint X=375.073 Y=72.4095 Z=0
    g342: GeomPoint X=371.073 Y=76.4095 Z=0
    g343: LineSegment StartX=322.073 StartY=76.4095 StartZ=0 EndX=371.073 EndY=76.4095 EndZ=0
    g344: LineSegment StartX=318.073 StartY=72.4095 StartZ=0 EndX=318.073 EndY=-47.4805 EndZ=0
    g345: LineSegment StartX=375.073 StartY=72.4095 StartZ=0 EndX=375.073 EndY=-78.7896 EndZ=0
    g346: ArcOfCircle CenterX=-26.9272 CenterY=22.1087 CenterZ=0 NormalX=0 NormalY=0 NormalZ=1 AngleXU=0 Radius=4 StartAngle=5e-16 EndAngle=3.14159
    g347: LineSegment StartX=-30.9272 StartY=22.1087 StartZ=0 EndX=-34.9272 EndY=-83.7794 EndZ=0
    g348: LineSegment StartX=-18.9272 StartY=-83.7794 StartZ=0 EndX=-22.9272 EndY=22.1087 EndZ=0
  constraints (572):
    c: Coincident(g0,g2)
    c: Block(g0)
    c: Block(g1)
    c: Vertical(g3)
    c: Vertical(g4)
    c: Block(g4)
    c: Block(g3)
    c: Tangent(g6,g7) = 1.5708
    c: Tangent(g7,g9) = 1.5708
    c: Equal(g6,g9)
    c: Coincident(g8,g6)
    c: Coincident(g8,g9)
    c: Block(g7)
    c: Block(g8)
    c: Weight(g10) = 1
    c: Equal(g10,g11)
    c: Equal(g10,g12)
    c: InternalAlignment(g10,g13)
    c: InternalAlignment(g11,g13)
    c: InternalAlignment(g12,g13)
    c: InternalAlignment(g14,g13)
    c: InternalAlignment(g15,g13)
    c: Weight(g16) = 1
    c: Equal(g16,g17)
    c: Equal(g16,g18)
    c: InternalAlignment(g16,g19)
    c: InternalAlignment(g17,g19)
    c: InternalAlignment(g18,g19)
    c: InternalAlignment(g20,g19)
    c: InternalAlignment(g21,g19)
    c: Block(g19)
    c: Block(g13)
    c: Weight(g22) = 1
    c: Equal(g22,g23)
    c: Equal(g22,g24)
    c: InternalAlignment(g22,g25)
    c: InternalAlignment(g23,g25)
    c: InternalAlignment(g24,g25)
    c: InternalAlignment(g26,g25)
    c: InternalAlignment(g27,g25)
    c: Weight(g28) = 1
    c: Equal(g28,g29)
    c: Equal(g28,g30)
    c: InternalAlignment(g28,g31)
    c: InternalAlignment(g29,g31)
    c: InternalAlignment(g30,g31)
    c: InternalAlignment(g32,g31)
    c: InternalAlignment(g33,g31)
    c: Block(g31)
    c: Block(g25)
    c: Weight(g34) = 1
    c: Equal(g34,g35)
    c: Equal(g34,g36)
    c: InternalAlignment(g34,g37)
    c: InternalAlignment(g35,g37)
    c: InternalAlignment(g36,g37)
    c: InternalAlignment(g38,g37)
    c: InternalAlignment(g39,g37)
    c: Weight(g40) = 1
    c: Equal(g40,g41)
    c: Equal(g40,g42)
    c: InternalAlignment(g40,g43)
    c: InternalAlignment(g41,g43)
    c: InternalAlignment(g42,g43)
    c: InternalAlignment(g44,g43)
    c: InternalAlignment(g45,g43)
    c: Block(g37)
    c: Block(g43)
    c: Coincident(g46,g4)
    c: Coincident(g46,g3)
    c: Horizontal(g46)
    c: Distance(g46) = 450
    c: Coincident(g47,g4)
    c: Coincident(g47,g3)
    c: Horizontal(g47)
    c: Horizontal(g48)
    c: Coincident(g2,g48)
    c: Block(g48)
    c: Coincident(g1,g48)
    c: Weight(g49) = 1
    c: Equal(g49,g50)
    c: Equal(g49,g51)
    c: InternalAlignment(g49,g52)
    c: InternalAlignment(g50,g52)
    c: InternalAlignment(g51,g52)
    c: InternalAlignment(g53,g52)
    c: InternalAlignment(g54,g52)
    c: Block(g52)
    c: Weight(g55) = 1
    c: Equal(g55,g56)
    c: Equal(g55,g57)
    c: InternalAlignment(g55,g58)
    c: InternalAlignment(g56,g58)
    c: InternalAlignment(g57,g58)
    c: InternalAlignment(g59,g58)
    c: InternalAlignment(g60,g58)
    c: Block(g58)
    c: Weight(g61) = 1
    c: Equal(g61,g62)
    c: Equal(g61,g63)
    c: InternalAlignment(g61,g64)
    c: InternalAlignment(g62,g64)
    c: InternalAlignment(g63,g64)
    c: InternalAlignment(g65,g64)
    c: InternalAlignment(g66,g64)
    c: Block(g64)
    c: Weight(g67) = 1
    c: Equal(g67,g68)
    c: Equal(g67,g69)
    c: InternalAlignment(g67,g70)
    c: InternalAlignment(g68,g70)
    c: InternalAlignment(g69,g70)
    c: InternalAlignment(g71,g70)
    c: InternalAlignment(g72,g70)
    c: Block(g70)
    c: Weight(g73) = 1
    c: Equal(g73,g74)
    c: Equal(g73,g75)
    c: InternalAlignment(g73,g76)
    c: InternalAlignment(g74,g76)
    c: InternalAlignment(g75,g76)
    c: InternalAlignment(g77,g76)
    c: InternalAlignment(g78,g76)
    c: Weight(g79) = 1
    c: Equal(g79,g80)
    c: Equal(g79,g81)
    c: InternalAlignment(g79,g82)
    c: InternalAlignment(g80,g82)
    c: InternalAlignment(g81,g82)
    c: InternalAlignment(g83,g82)
    c: InternalAlignment(g84,g82)
    c: Block(g76)
    c: Block(g82)
    c: Coincident(g85,g76)
    c: Coincident(g85,g82)
    c: Vertical(g85)
    c: Coincident(g86,g76)
    c: Coincident(g86,g58)
    c: Coincident(g87,g58)
    c: Coincident(g87,g82)
    c: Weight(g88) = 1
    c: Equal(g88,g89)
    c: Equal(g88,g90)
    c: InternalAlignment(g88,g91)
    c: InternalAlignment(g89,g91)
    c: InternalAlignment(g90,g91)
    c: InternalAlignment(g92,g91)
    c: InternalAlignment(g93,g91)
    c: Weight(g94) = 1
    c: Equal(g94,g95)
    c: Equal(g94,g96)
    c: InternalAlignment(g94,g97)
    c: InternalAlignment(g95,g97)
    c: InternalAlignment(g96,g97)
    c: InternalAlignment(g98,g97)
    c: InternalAlignment(g99,g97)
    c: Block(g91)
    c: Block(g97)
    c: Coincident(g100,g91)
    c: Coincident(g100,g97)
    c: Vertical(g100)
    c: Coincident(g101,g91)
    c: Coincident(g101,g52)
    c: Coincident(g102,g52)
    c: Coincident(g102,g97)
    c: Weight(g103) = 1
    c: Equal(g103,g104)
    c: Equal(g103,g105)
    c: InternalAlignment(g103,g106)
    c: InternalAlignment(g104,g106)
    c: InternalAlignment(g105,g106)
    c: InternalAlignment(g107,g106)
    c: InternalAlignment(g108,g106)
    c: Weight(g109) = 1
    c: Equal(g109,g110)
    c: Equal(g109,g111)
    c: InternalAlignment(g109,g112)
    c: InternalAlignment(g110,g112)
    c: InternalAlignment(g111,g112)
    c: InternalAlignment(g113,g112)
    c: InternalAlignment(g114,g112)
    c: Block(g106)
    c: Block(g112)
    c: Coincident(g115,g106)
    c: Coincident(g115,g112)
    c: Vertical(g115)
    c: Coincident(g116,g112)
    c: Coincident(g116,g70)
    c: Coincident(g117,g70)
    c: Coincident(g117,g106)
    c: Weight(g118) = 1
    c: Equal(g118,g119)
    c: Equal(g118,g120)
    c: InternalAlignment(g118,g121)
    c: InternalAlignment(g119,g121)
    c: InternalAlignment(g120,g121)
    c: InternalAlignment(g122,g121)
    c: InternalAlignment(g123,g121)
    c: Weight(g124) = 1
    c: Equal(g124,g125)
    c: Equal(g124,g126)
    c: InternalAlignment(g124,g127)
    c: InternalAlignment(g125,g127)
    c: InternalAlignment(g126,g127)
    c: InternalAlignment(g128,g127)
    c: InternalAlignment(g129,g127)
    c: Block(g121)
    c: Block(g127)
    c: Coincident(g130,g121)
    c: Coincident(g130,g127)
    c: Vertical(g130)
    c: Coincident(g131,g127)
    c: Coincident(g131,g64)
    c: Coincident(g132,g64)
    c: Coincident(g132,g121)
    c: Weight(g133) = 1
    c: Equal(g133,g134)
    c: Equal(g133,g135)
    c: InternalAlignment(g133,g136)
    c: InternalAlignment(g134,g136)
    c: InternalAlignment(g135,g136)
    c: InternalAlignment(g137,g136)
    c: InternalAlignment(g138,g136)
    c: Weight(g139) = 1
    c: Equal(g139,g140)
    c: Equal(g139,g141)
    c: InternalAlignment(g139,g142)
    c: InternalAlignment(g140,g142)
    c: InternalAlignment(g141,g142)
    c: InternalAlignment(g143,g142)
    c: InternalAlignment(g144,g142)
    c: Weight(g145) = 1
    c: Equal(g145,g146)
    c: Equal(g145,g147)
    c: InternalAlignment(g145,g148)
    c: InternalAlignment(g146,g148)
    c: InternalAlignment(g147,g148)
    c: InternalAlignment(g149,g148)
    c: InternalAlignment(g150,g148)
    c: Weight(g151) = 1
    c: Equal(g151,g152)
    c: Equal(g151,g153)
    c: InternalAlignment(g151,g154)
    c: InternalAlignment(g152,g154)
    c: InternalAlignment(g153,g154)
    c: InternalAlignment(g155,g154)
    c: InternalAlignment(g156,g154)
    c: Block(g154)
    c: Block(g148)
    c: Block(g142)
    c: Block(g136)
    c: Coincident(g157,g31)
    c: Coincident(g157,g154)
    c: Coincident(g158,g154)
    c: Coincident(g158,g148)
    c: Horizontal(g158)
    c: Coincident(g159,g148)
    c: Coincident(g159,g31)
    c: Vertical(g159)
    c: Coincident(g160,g25)
    c: Coincident(g160,g142)
    c: Vertical(g160)
    c: Coincident(g161,g142)
    c: Coincident(g161,g136)
    c: Horizontal(g161)
    c: Coincident(g162,g136)
    c: Coincident(g162,g25)
    c: Weight(g163) = 1
    c: Equal(g163,g164)
    c: Equal(g163,g165)
    c: InternalAlignment(g163,g166)
    c: InternalAlignment(g164,g166)
    c: InternalAlignment(g165,g166)
    c: InternalAlignment(g167,g166)
    c: InternalAlignment(g168,g166)
    c: Weight(g169) = 1
    c: Equal(g169,g170)
    c: Equal(g169,g171)
    c: InternalAlignment(g169,g172)
    c: InternalAlignment(g170,g172)
    c: InternalAlignment(g171,g172)
    c: InternalAlignment(g173,g172)
    c: InternalAlignment(g174,g172)
    c: Weight(g175) = 1
    c: Equal(g175,g176)
    c: Equal(g175,g177)
    c: InternalAlignment(g175,g178)
    c: InternalAlignment(g176,g178)
    c: InternalAlignment(g177,g178)
    c: InternalAlignment(g179,g178)
    c: InternalAlignment(g180,g178)
    c: Weight(g181) = 1
    c: Equal(g181,g182)
    c: Equal(g181,g183)
    c: InternalAlignment(g181,g184)
    c: InternalAlignment(g182,g184)
    c: InternalAlignment(g183,g184)
    c: InternalAlignment(g185,g184)
    c: InternalAlignment(g186,g184)
    c: Block(g184)
    c: Block(g178)
    c: Block(g172)
    c: Block(g166)
    c: Coincident(g187,g184)
    c: Coincident(g187,g178)
    c: Horizontal(g187)
    c: Coincident(g188,g178)
    c: Coincident(g188,g13)
    c: Vertical(g188)
    c: Coincident(g189,g19)
    c: Coincident(g189,g172)
    c: Vertical(g189)
    c: Coincident(g190,g172)
    c: Coincident(g190,g166)
    c: Horizontal(g190)
    c: Coincident(g191,g166)
    c: Coincident(g191,g19)
    c: Coincident(g192,g13)
    c: Weight(g193) = 1
    c: Equal(g193,g194)
    c: Equal(g193,g195)
    c: InternalAlignment(g193,g196)
    c: InternalAlignment(g194,g196)
    c: InternalAlignment(g195,g196)
    c: InternalAlignment(g197,g196)
    c: InternalAlignment(g198,g196)
    c: Weight(g199) = 1
    c: Equal(g199,g200)
    c: Equal(g199,g201)
    c: InternalAlignment(g199,g202)
    c: InternalAlignment(g200,g202)
    c: InternalAlignment(g201,g202)
    c: InternalAlignment(g203,g202)
    c: InternalAlignment(g204,g202)
    c: Block(g202)
    c: Block(g196)
    c: Coincident(g205,g202)
    c: Coincident(g205,g37)
    c: Coincident(g206,g37)
    c: Coincident(g206,g196)
    c: Coincident(g207,g196)
    c: Coincident(g207,g202)
    c: Vertical(g207)
    c: Weight(g208) = 1
    c: Equal(g208,g209)
    c: Equal(g208,g210)
    c: InternalAlignment(g208,g211)
    c: InternalAlignment(g209,g211)
    c: InternalAlignment(g210,g211)
    c: InternalAlignment(g212,g211)
    c: InternalAlignment(g213,g211)
    c: Weight(g214) = 1
    c: Equal(g214,g215)
    c: Equal(g214,g216)
    c: InternalAlignment(g214,g217)
    c: InternalAlignment(g215,g217)
    c: InternalAlignment(g216,g217)
    c: InternalAlignment(g218,g217)
    c: InternalAlignment(g219,g217)
    c: Block(g217)
    c: Block(g211)
    c: Coincident(g220,g211)
    c: Coincident(g220,g43)
    c: Coincident(g221,g43)
    c: Coincident(g221,g217)
    c: Coincident(g222,g217)
    c: Coincident(g222,g211)
    c: Vertical(g222)
    c: Horizontal(g223)
    c: Block(g223)
    c: Vertical(g224)
    c: Block(g224)
    c: Block(g225)
    c: Weight(g226) = 1
    c: Equal(g226,g227)
    c: Equal(g226,g228)
    c: InternalAlignment(g226,g229)
    c: InternalAlignment(g227,g229)
    c: InternalAlignment(g228,g229)
    c: InternalAlignment(g230,g229)
    c: InternalAlignment(g231,g229)
    c: Weight(g232) = 1
    c: Equal(g232,g233)
    c: Equal(g232,g234)
    c: InternalAlignment(g232,g235)
    c: InternalAlignment(g233,g235)
    c: InternalAlignment(g234,g235)
    c: InternalAlignment(g236,g235)
    c: InternalAlignment(g237,g235)
    c: Weight(g238) = 1
    c: Equal(g238,g239)
    c: Equal(g238,g240)
    c: InternalAlignment(g238,g241)
    c: InternalAlignment(g239,g241)
    c: InternalAlignment(g240,g241)
    c: InternalAlignment(g242,g241)
    c: InternalAlignment(g243,g241)
    c: Weight(g244) = 1
    c: Equal(g244,g245)
    c: Equal(g244,g246)
    c: InternalAlignment(g244,g247)
    c: InternalAlignment(g245,g247)
    c: InternalAlignment(g246,g247)
    c: InternalAlignment(g248,g247)
    c: InternalAlignment(g249,g247)
    c: Block(g229)
    c: Block(g235)
    c: Block(g241)
    c: Block(g247)
    c: Coincident(g250,g235)
    c: Coincident(g250,g229)
    c: Horizontal(g250)
    c: Block(g192)
    c: Weight(g251) = 1
    c: Equal(g251,g252)
    c: Equal(g251,g253)
    c: InternalAlignment(g251,g254)
    c: InternalAlignment(g252,g254)
    c: InternalAlignment(g253,g254)
    c: InternalAlignment(g255,g254)
    c: InternalAlignment(g256,g254)
    c: Weight(g257) = 1
    c: Equal(g257,g258)
    c: Equal(g257,g259)
    c: InternalAlignment(g257,g260)
    c: InternalAlignment(g258,g260)
    c: InternalAlignment(g259,g260)
    c: InternalAlignment(g261,g260)
    c: InternalAlignment(g262,g260)
    c: Block(g254)
    c: Block(g260)
    c: Coincident(g263,g254)
    c: Coincident(g263,g260)
    c: Weight(g264) = 1
    c: Equal(g264,g265)
    c: Equal(g264,g266)
    c: InternalAlignment(g264,g267)
    c: InternalAlignment(g265,g267)
    c: InternalAlignment(g266,g267)
    c: InternalAlignment(g268,g267)
    c: InternalAlignment(g269,g267)
    c: Weight(g270) = 1
    c: Equal(g270,g271)
    c: Equal(g270,g272)
    c: InternalAlignment(g270,g273)
    c: InternalAlignment(g271,g273)
    c: InternalAlignment(g272,g273)
    c: InternalAlignment(g274,g273)
    c: InternalAlignment(g275,g273)
    c: Weight(g276) = 1
    c: Equal(g276,g277)
    c: Equal(g276,g278)
    c: InternalAlignment(g276,g279)
    c: InternalAlignment(g277,g279)
    c: InternalAlignment(g278,g279)
    c: InternalAlignment(g280,g279)
    c: InternalAlignment(g281,g279)
    c: Block(g279)
    c: Block(g273)
    c: Block(g267)
    c: Coincident(g282,g273)
    c: Coincident(g282,g267)
    c: Coincident(g283,g267)
    c: Coincident(g283,g279)
    c: Vertical(g283)
    c: Coincident(g284,g279)
    c: Coincident(g284,g273)
    c: Horizontal(g284)
    c: Weight(g285) = 1
    c: Equal(g285,g286)
    c: InternalAlignment(g285,g287)
    c: InternalAlignment(g286,g287)
    c: InternalAlignment(g288,g287)
    c: InternalAlignment(g289,g287)
    c: Weight(g290) = 1
    c: InternalAlignment(g291,g293)
    c: InternalAlignment(g292,g293)
    c: InternalAlignment(g294,g293)
    c: InternalAlignment(g295,g293)
    c: Weight(g296) = 1
    c: Equal(g296,g297)
    c: Equal(g296,g298)
    c: InternalAlignment(g296,g299)
    c: InternalAlignment(g297,g299)
    c: InternalAlignment(g298,g299)
    c: InternalAlignment(g300,g299)
    c: InternalAlignment(g301,g299)
    c: Equal(g302,g303)
    c: Equal(g302,g304)
    c: InternalAlignment(g302,g305)
    c: InternalAlignment(g303,g305)
    c: InternalAlignment(g304,g305)
    c: InternalAlignment(g306,g305)
    c: InternalAlignment(g307,g305)
    c: Block(g293)
    c: Block(g299)
    c: Block(g305)
    c: Block(g287)
    c: Coincident(g308,g287)
    c: Coincident(g308,g293)
    c: Horizontal(g308)
    c: Coincident(g309,g293)
    c: Coincident(g309,g299)
    c: Vertical(g309)
    c: Coincident(g310,g299)
    c: Coincident(g310,g305)
    c: Horizontal(g310)
    c: Coincident(g311,g305)
    c: Coincident(g311,g287)
    c: Weight(g312) = 1
    c: Equal(g312,g313)
    c: Equal(g312,g314)
    c: InternalAlignment(g312,g315)
    c: InternalAlignment(g313,g315)
    c: InternalAlignment(g314,g315)
    c: InternalAlignment(g316,g315)
    c: InternalAlignment(g317,g315)
    c: Weight(g318) = 1
    c: Equal(g318,g319)
    c: Equal(g318,g320)
    c: InternalAlignment(g318,g321)
    c: InternalAlignment(g319,g321)
    c: InternalAlignment(g320,g321)
    c: InternalAlignment(g322,g321)
    c: InternalAlignment(g323,g321)
    c: Weight(g324) = 1
    c: Equal(g324,g325)
    c: Equal(g324,g326)
    c: InternalAlignment(g324,g327)
    c: InternalAlignment(g325,g327)
    c: InternalAlignment(g326,g327)
    c: InternalAlignment(g328,g327)
    c: InternalAlignment(g329,g327)
    c: Block(g327)
    c: Block(g321)
    c: Block(g315)
    c: Coincident(g330,g327)
    c: Coincident(g330,g321)
    c: Horizontal(g330)
    c: Coincident(g331,g321)
    c: Coincident(g331,g315)
    c: Vertical(g331)
    c: Coincident(g332,g315)
    c: Coincident(g332,g327)
    c: InternalAlignment(g333,g334)
    c: InternalAlignment(g335,g334)
    c: InternalAlignment(g336,g334)
    c: Block(g334)
    c: Equal(g337,g338)
    c: Equal(g337,g339)
    c: InternalAlignment(g337,g340)
    c: InternalAlignment(g338,g340)
    c: InternalAlignment(g339,g340)
    c: InternalAlignment(g341,g340)
    c: InternalAlignment(g342,g340)
    c: Block(g340)
    c: Coincident(g343,g334)
    c: Horizontal(g343)
    c: Block(g343)
    c: Coincident(g344,g334)
    c: Coincident(g344,g260)
    c: Vertical(g344)
    c: Coincident(g345,g340)
    c: Coincident(g345,g254)
    c: Vertical(g345)
    c: Coincident(g347,g5)
    c: Coincident(g348,g5)
    c: Block(g346)
    c: Block(g5)
    c: Block(g348)
    c: Block(g347)
    c: Distance(g344) = 119.89
FEATURE [Sketcher::SketchObject] Sketch001
  FullyConstrained = true
  MapMode = 4
  Placement = pos=(0,0,0) rot=(0.57735,0.57735,0.57735;2.0944rad)
  Support = -> [Sketch]
  sketch-geometry (46):
    g0: BSplineCurve PolesCount=3 KnotsCount=2 Degree=2 IsPeriodic=0
    g1: ArcOfCircle CenterX=73.1223 CenterY=-32.291 CenterZ=0 NormalX=0 NormalY=0 NormalZ=1 AngleXU=0 Radius=13 StartAngle=5.92268 EndAngle=9.06428
    g2: ArcOfCircle CenterX=66.7816 CenterY=-49.1439 CenterZ=0 NormalX=0 NormalY=0 NormalZ=1 AngleXU=0 Radius=13 StartAngle=2.78068 EndAngle=5.92131
    g3: ArcOfCircle CenterX=55.9263 CenterY=-78.1807 CenterZ=0 NormalX=0 NormalY=0 NormalZ=1 AngleXU=0 Radius=13 StartAngle=5.92268 EndAngle=9.06428
    g4: ArcOfCircle CenterX=49.5884 CenterY=-95.0342 CenterZ=0 NormalX=0 NormalY=0 NormalZ=1 AngleXU=0 Radius=13 StartAngle=2.78068 EndAngle=5.92131
    g5: ArcOfCircle CenterX=38.7206 CenterY=-124.067 CenterZ=0 NormalX=0 NormalY=0 NormalZ=1 AngleXU=0 Radius=13 StartAngle=5.92268 EndAngle=9.06428
    g6: ArcOfCircle CenterX=32.3875 CenterY=-140.92 CenterZ=0 NormalX=0 NormalY=0 NormalZ=1 AngleXU=0 Radius=13 StartAngle=2.78068 EndAngle=5.92131
    g7: ArcOfCircle CenterX=21.4715 CenterY=-169.934 CenterZ=0 NormalX=0 NormalY=0 NormalZ=1 AngleXU=0 Radius=13 StartAngle=5.92268 EndAngle=9.06428
    g8: ArcOfCircle CenterX=15.1336 CenterY=-186.787 CenterZ=0 NormalX=0 NormalY=0 NormalZ=1 AngleXU=0 Radius=13 StartAngle=2.78068 EndAngle=5.92131
    g9-g12: Circle x4 (B-spline internal-alignment scaffolding for g13; pole/knot coordinates omitted)
    g13: BSplineCurve PolesCount=4 KnotsCount=2 Degree=3 IsPeriodic=0
    g14: GeomPoint X=28.8094 Y=-19.0875 Z=0
    g15: GeomPoint X=47.0443 Y=-50.4712 Z=0
    g16: Circle CenterX=53.5586 CenterY=-23.2695 CenterZ=0 NormalX=0 NormalY=0 NormalZ=1 AngleXU=0 Radius=3.24518
    g17: Circle CenterX=-195.441 CenterY=-127.082 CenterZ=0 NormalX=0 NormalY=0 NormalZ=1 AngleXU=0 Radius=1
    g18: Circle CenterX=-8.24091 CenterY=-197.481 CenterZ=0 NormalX=0 NormalY=0 NormalZ=1 AngleXU=0 Radius=1
    g19: Circle CenterX=12.8789 CenterY=-141.321 CenterZ=0 NormalX=0 NormalY=0 NormalZ=1 AngleXU=0 Radius=1
    g20: BSplineCurve PolesCount=3 KnotsCount=2 Degree=2 IsPeriodic=0
    g21: GeomPoint X=-195.441 Y=-127.082 Z=0
    g22: GeomPoint X=12.8789 Y=-141.321 Z=0
    g23: Circle CenterX=-12.8016 CenterY=-179.036 CenterZ=0 NormalX=0 NormalY=0 NormalZ=1 AngleXU=0 Radius=10.5072
    g24: Circle CenterX=0.933922 CenterY=-166.43 CenterZ=0 NormalX=0 NormalY=0 NormalZ=1 AngleXU=0 Radius=3.26661
    g25: Circle CenterX=-33.5518 CenterY=-176.44 CenterZ=0 NormalX=0 NormalY=0 NormalZ=1 AngleXU=0 Radius=5.64388
    g26: Circle CenterX=-47.2366 CenterY=-173.859 CenterZ=0 NormalX=0 NormalY=0 NormalZ=1 AngleXU=0 Radius=3.01653
    g27: Circle CenterX=-56.2595 CenterY=-171.456 CenterZ=0 NormalX=0 NormalY=0 NormalZ=1 AngleXU=0 Radius=2.12826
    g28: ArcOfCircle CenterX=51.2151 CenterY=-198.473 CenterZ=0 NormalX=0 NormalY=0 NormalZ=1 AngleXU=0 Radius=20 StartAngle=2.78189 EndAngle=4.35269
    g29: LineSegment StartX=32.4951 StartY=-191.433 StartZ=0 EndX=94.6578 EndY=-26.1352 EndZ=0
    g30: LineSegment StartX=43.1192 StartY=-220.001 StartZ=0 EndX=-196.497 EndY=-129.89 EndZ=0
    g31: LineSegment StartX=43.1192 StartY=-220.001 StartZ=0 EndX=44.1752 EndY=-217.193 EndZ=0
    g32: LineSegment StartX=117.223 StartY=-19.0875 StartZ=0 EndX=117.223 EndY=-16.0875 EndZ=0
    g33: LineSegment StartX=117.223 StartY=-16.0875 StartZ=0 EndX=17.2232 EndY=-16.0875 EndZ=0
    g34: LineSegment StartX=17.2232 StartY=-16.0875 StartZ=0 EndX=17.2232 EndY=-19.0875 EndZ=0
    g35: LineSegment StartX=28.8094 StartY=-19.0875 StartZ=0 EndX=17.2232 EndY=-19.0875 EndZ=0
    g36: LineSegment StartX=47.0443 StartY=-50.4712 StartZ=0 EndX=12.8789 EndY=-141.321 EndZ=0
    g37: LineSegment StartX=-195.441 StartY=-127.082 StartZ=0 EndX=-196.497 EndY=-129.89 EndZ=0
    g38: LineSegment StartX=85.2866 StartY=-36.8766 StartZ=0 EndX=78.9396 EndY=-53.7463 EndZ=0
    g39: LineSegment StartX=60.9579 StartY=-27.7053 StartZ=0 EndX=54.6191 EndY=-44.5532 EndZ=0
    g40: LineSegment StartX=68.0907 StartY=-82.7664 StartZ=0 EndX=61.7465 EndY=-99.6365 EndZ=0
    g41: LineSegment StartX=43.7619 StartY=-73.595 StartZ=0 EndX=37.426 EndY=-90.4435 EndZ=0
    g42: LineSegment StartX=50.885 StartY=-128.652 StartZ=0 EndX=44.5456 EndY=-145.522 EndZ=0
    g43: LineSegment StartX=26.5562 StartY=-119.481 StartZ=0 EndX=20.2251 EndY=-136.329 EndZ=0
    g44: LineSegment StartX=9.3071 StartY=-165.349 StartZ=0 EndX=2.97115 EndY=-182.197 EndZ=0
    g45: LineSegment StartX=33.6358 StartY=-174.52 StartZ=0 EndX=27.2917 EndY=-191.39 EndZ=0
  constraints (71):
    c: Block(g0)
    c: Block(g1)
    c: Block(g2)
    c: Block(g4)
    c: Block(g3)
    c: Block(g6)
    c: Block(g5)
    c: Block(g8)
    c: Block(g7)
    c: Weight(g9) = 1
    c: Equal(g9,g10)
    c: Equal(g9,g11)
    c: Equal(g9,g12)
    c: InternalAlignment(g9-g12 -> g13) x4
    c: InternalAlignment(g14,g13)
    c: InternalAlignment(g15,g13)
    c: Block(g16)
    c: Weight(g17) = 1
    c: Equal(g17,g18)
    c: Equal(g17,g19)
    c: InternalAlignment(g17,g20)
    c: InternalAlignment(g18,g20)
    c: InternalAlignment(g19,g20)
    c: InternalAlignment(g21,g20)
    c: InternalAlignment(g22,g20)
    c: Block(g20)
    c: Block(g23)
    c: Block(g24)
    c: Block(g25)
    c: Block(g26)
    c: Block(g27)
    c: Block(g28)
    c: Coincident(g29,g28)
    c: Coincident(g29,g0)
    c: Block(g13)
    c: Coincident(g31,g30)
    c: Coincident(g31,g28)
    c: Block(g31)
    c: Coincident(g32,g0)
    c: Vertical(g32)
    c: Coincident(g33,g32)
    c: Horizontal(g33)
    c: Coincident(g34,g33)
    c: Vertical(g34)
    c: Block(g33)
    c: Coincident(g35,g13)
    c: Coincident(g35,g34)
    c: Horizontal(g35)
    c: Coincident(g36,g13)
    c: Coincident(g36,g20)
    c: Coincident(g37,g20)
    c: Coincident(g37,g30)
    c: Block(g30)
    c: Coincident(g38,g1)
    c: Coincident(g38,g2)
    c: Coincident(g39,g1)
    c: Coincident(g39,g2)
    c: Coincident(g40,g3)
    c: Coincident(g40,g4)
    c: Coincident(g41,g3)
    c: Coincident(g41,g4)
    c: Coincident(g42,g5)
    c: Coincident(g42,g6)
    c: Coincident(g43,g5)
    c: Coincident(g43,g6)
    c: Coincident(g44,g7)
    c: Coincident(g44,g8)
    c: Coincident(g45,g7)
    c: Coincident(g45,g8)
    c: Distance(g30) = 256
    c: Distance(g33) = 100
FEATURE [Part::Extrusion] Extrude002
  Base = -> Sketch001
  Dir = (1,0,0)
  DirMode = 2
  FaceMakerClass = Part::FaceMakerBullseye
  LengthFwd = 8
  LengthRev = 0
  Solid = true
  Symmetric = false
FEATURE [Sketcher::SketchObject] Sketch002
  FullyConstrained = true
  sketch-geometry (20):
    g0: LineSegment StartX=-2.77179 StartY=-200.304 StartZ=0 EndX=5.22821 EndY=-200.304 EndZ=0
    g1: LineSegment StartX=5.22821 StartY=-200.304 StartZ=0 EndX=5.22821 EndY=-197.304 EndZ=0
    g2: LineSegment StartX=-2.77179 StartY=-200.304 StartZ=0 EndX=-2.77179 EndY=-197.304 EndZ=0
    g3: LineSegment StartX=5.22821 StartY=-197.304 StartZ=0 EndX=8.22821 EndY=-197.304 EndZ=0
    g4: LineSegment StartX=-2.77179 StartY=-197.304 StartZ=0 EndX=-5.77179 EndY=-197.304 EndZ=0
    g5: LineSegment StartX=19.2282 StartY=-203.304 StartZ=0 EndX=19.2282 EndY=-206.304 EndZ=0
    g6: LineSegment StartX=-16.7718 StartY=-203.304 StartZ=0 EndX=-16.7718 EndY=-206.304 EndZ=0
    g7: LineSegment StartX=-16.7718 StartY=-206.304 StartZ=0 EndX=19.2282 EndY=-206.304 EndZ=0
    g8: Circle CenterX=-16.7718 CenterY=-203.304 CenterZ=0 NormalX=0 NormalY=0 NormalZ=1 AngleXU=0 Radius=1
    g9: Circle CenterX=-5.77179 CenterY=-203.304 CenterZ=0 NormalX=0 NormalY=0 NormalZ=1 AngleXU=0 Radius=1
    g10: Circle CenterX=-5.77179 CenterY=-197.304 CenterZ=0 NormalX=0 NormalY=0 NormalZ=1 AngleXU=0 Radius=1
    g11: BSplineCurve PolesCount=3 KnotsCount=2 Degree=2 IsPeriodic=0
    g12: GeomPoint X=-16.7718 Y=-203.304 Z=0
    g13: GeomPoint X=-5.77179 Y=-197.304 Z=0
    g14: Circle CenterX=19.2282 CenterY=-203.304 CenterZ=0 NormalX=0 NormalY=0 NormalZ=1 AngleXU=0 Radius=1
    g15: Circle CenterX=8.22821 CenterY=-203.304 CenterZ=0 NormalX=0 NormalY=0 NormalZ=1 AngleXU=0 Radius=1
    g16: Circle CenterX=8.22821 CenterY=-197.304 CenterZ=0 NormalX=0 NormalY=0 NormalZ=1 AngleXU=0 Radius=1
    g17: BSplineCurve PolesCount=3 KnotsCount=2 Degree=2 IsPeriodic=0
    g18: GeomPoint X=19.2282 Y=-203.304 Z=0
    g19: GeomPoint X=8.22821 Y=-197.304 Z=0
  constraints (41):
    c: Horizontal(g0)
    c: Distance(g0) = 8
    c: Coincident(g1,g0)
    c: Vertical(g1)
    c: Distance(g1) = 3
    c: Coincident(g2,g0)
    c: Vertical(g2)
    c: Distance(g2) = 3
    c: Coincident(g3,g1)
    c: Horizontal(g3)
    c: Distance(g3) = 3
    c: Coincident(g4,g2)
    c: Horizontal(g4)
    c: Distance(g4) = 3
    c: Vertical(g5)
    c: Vertical(g6)
    c: Coincident(g7,g6)
    c: Coincident(g7,g5)
    c: Weight(g8) = 1
    c: Equal(g8,g9)
    c: Equal(g8,g10)
    c: Coincident(g11,g4)
    c: InternalAlignment(g8,g11)
    c: InternalAlignment(g9,g11)
    c: InternalAlignment(g10,g11)
    c: InternalAlignment(g12,g11)
    c: InternalAlignment(g13,g11)
    c: Coincident(g17,g5)
    c: Weight(g14) = 1
    c: Equal(g14,g15)
    c: Equal(g14,g16)
    c: Coincident(g17,g3)
    c: InternalAlignment(g14,g17)
    c: InternalAlignment(g15,g17)
    c: InternalAlignment(g16,g17)
    c: InternalAlignment(g18,g17)
    c: InternalAlignment(g19,g17)
    c: Block(g7)
    c: Block(g17)
    c: Block(g11)
    c: Block(g6)
FEATURE [Part::Extrusion] Extrude003
  Base = -> Sketch002
  Dir = (0,0,1)
  DirMode = 2
  FaceMakerClass = Part::FaceMakerBullseye
  LengthFwd = 260
  LengthRev = 0
  Solid = true
  Symmetric = false
FEATURE [Sketcher::SketchObject] Sketch003
  FullyConstrained = false
  sketch-geometry (410):
    g0: LineSegment StartX=-42.9272 StartY=136.221 StartZ=0 EndX=-42.9272 EndY=-103.779 EndZ=0
    g1: LineSegment StartX=407.073 StartY=136.221 StartZ=0 EndX=407.073 EndY=-103.779 EndZ=0
    g2: ArcOfCircle CenterX=-26.9272 CenterY=-83.7794 CenterZ=0 NormalX=0 NormalY=0 NormalZ=1 AngleXU=0 Radius=8 StartAngle=3.14159 EndAngle=6.28319
    g3: ArcOfCircle CenterX=391.073 CenterY=-83.7794 CenterZ=0 NormalX=0 NormalY=0 NormalZ=1 AngleXU=0 Radius=8 StartAngle=3.14159 EndAngle=6.28319
    g4: Circle CenterX=175.022 CenterY=27.0628 CenterZ=0 NormalX=0 NormalY=0 NormalZ=1 AngleXU=0 Radius=1
    g5: Circle CenterX=179.022 CenterY=24.8665 CenterZ=0 NormalX=0 NormalY=0 NormalZ=1 AngleXU=0 Radius=1
    g6: Circle CenterX=179.022 CenterY=27.0628 CenterZ=0 NormalX=0 NormalY=0 NormalZ=1 AngleXU=0 Radius=1
    g7: BSplineCurve PolesCount=3 KnotsCount=2 Degree=2 IsPeriodic=0
    g8: GeomPoint X=175.022 Y=27.0628 Z=0
    g9: GeomPoint X=179.022 Y=27.0628 Z=0
    g10: Circle CenterX=189.124 CenterY=27.0628 CenterZ=0 NormalX=0 NormalY=0 NormalZ=1 AngleXU=0 Radius=1
    g11: Circle CenterX=185.124 CenterY=24.8665 CenterZ=0 NormalX=0 NormalY=0 NormalZ=1 AngleXU=0 Radius=1
    g12: Circle CenterX=185.124 CenterY=27.0628 CenterZ=0 NormalX=0 NormalY=0 NormalZ=1 AngleXU=0 Radius=1
    g13: BSplineCurve PolesCount=3 KnotsCount=2 Degree=2 IsPeriodic=0
    g14: GeomPoint X=189.124 Y=27.0628 Z=0
    g15: GeomPoint X=185.124 Y=27.0628 Z=0
    g16: Circle CenterX=175.022 CenterY=5.37834 CenterZ=0 NormalX=0 NormalY=0 NormalZ=1 AngleXU=0 Radius=1
    g17: Circle CenterX=179.022 CenterY=7.57463 CenterZ=0 NormalX=0 NormalY=0 NormalZ=1 AngleXU=0 Radius=1
    g18: Circle CenterX=179.022 CenterY=5.34704 CenterZ=0 NormalX=0 NormalY=0 NormalZ=1 AngleXU=0 Radius=1
    g19: BSplineCurve PolesCount=3 KnotsCount=2 Degree=2 IsPeriodic=0
    g20: GeomPoint X=175.022 Y=5.37834 Z=0
    g21: GeomPoint X=179.022 Y=5.34704 Z=0
    g22: Circle CenterX=189.124 CenterY=5.37834 CenterZ=0 NormalX=0 NormalY=0 NormalZ=1 AngleXU=0 Radius=1
    g23: Circle CenterX=185.124 CenterY=7.57463 CenterZ=0 NormalX=0 NormalY=0 NormalZ=1 AngleXU=0 Radius=1
    g24: Circle CenterX=185.124 CenterY=5.34704 CenterZ=0 NormalX=0 NormalY=0 NormalZ=1 AngleXU=0 Radius=1
    g25: BSplineCurve PolesCount=3 KnotsCount=2 Degree=2 IsPeriodic=0
    g26: GeomPoint X=189.124 Y=5.37834 Z=0
    g27: GeomPoint X=185.124 Y=5.34704 Z=0
    g28: Circle CenterX=165.871 CenterY=18.1458 CenterZ=0 NormalX=0 NormalY=0 NormalZ=1 AngleXU=0 Radius=1
    g29: Circle CenterX=169.377 CenterY=16.2206 CenterZ=0 NormalX=0 NormalY=0 NormalZ=1 AngleXU=0 Radius=1
    g30: Circle CenterX=165.871 CenterY=14.2954 CenterZ=0 NormalX=0 NormalY=0 NormalZ=1 AngleXU=0 Radius=1
    g31: BSplineCurve PolesCount=3 KnotsCount=2 Degree=2 IsPeriodic=0
    g32: GeomPoint X=165.871 Y=18.1458 Z=0
    g33: GeomPoint X=165.871 Y=14.2954 Z=0
    g34: Circle CenterX=198.275 CenterY=18.1458 CenterZ=0 NormalX=0 NormalY=0 NormalZ=1 AngleXU=0 Radius=1
    g35: Circle CenterX=194.768 CenterY=16.2206 CenterZ=0 NormalX=0 NormalY=0 NormalZ=1 AngleXU=0 Radius=1
    g36: Circle CenterX=198.275 CenterY=14.2954 CenterZ=0 NormalX=0 NormalY=0 NormalZ=1 AngleXU=0 Radius=1
    g37: BSplineCurve PolesCount=3 KnotsCount=2 Degree=2 IsPeriodic=0
    g38: GeomPoint X=198.275 Y=18.1458 Z=0
    g39: GeomPoint X=198.275 Y=14.2954 Z=0
    g40: LineSegment StartX=407.073 StartY=-103.779 StartZ=0 EndX=-42.9272 EndY=-103.779 EndZ=0
    g41: Circle CenterX=125.607 CenterY=54.1951 CenterZ=0 NormalX=0 NormalY=0 NormalZ=1 AngleXU=0 Radius=1
    g42: Circle CenterX=139.632 CenterY=46.4944 CenterZ=0 NormalX=0 NormalY=0 NormalZ=1 AngleXU=0 Radius=1
    g43: Circle CenterX=127.326 CenterY=56.7187 CenterZ=0 NormalX=0 NormalY=0 NormalZ=1 AngleXU=0 Radius=1
    g44: BSplineCurve PolesCount=3 KnotsCount=2 Degree=2 IsPeriodic=0
    g45: GeomPoint X=125.607 Y=54.1951 Z=0
    g46: GeomPoint X=127.326 Y=56.7187 Z=0
    g47: Circle CenterX=236.821 CenterY=56.7187 CenterZ=0 NormalX=0 NormalY=0 NormalZ=1 AngleXU=0 Radius=1
    g48: Circle CenterX=224.513 CenterY=46.4944 CenterZ=0 NormalX=0 NormalY=0 NormalZ=1 AngleXU=0 Radius=1
    g49: Circle CenterX=238.538 CenterY=54.1951 CenterZ=0 NormalX=0 NormalY=0 NormalZ=1 AngleXU=0 Radius=1
    g50: BSplineCurve PolesCount=3 KnotsCount=2 Degree=2 IsPeriodic=0
    g51: GeomPoint X=236.821 Y=56.7187 Z=0
    g52: GeomPoint X=238.538 Y=54.1951 Z=0
    g53: Circle CenterX=238.538 CenterY=-21.7539 CenterZ=0 NormalX=0 NormalY=0 NormalZ=1 AngleXU=0 Radius=1
    g54: Circle CenterX=224.513 CenterY=-14.0532 CenterZ=0 NormalX=0 NormalY=0 NormalZ=1 AngleXU=0 Radius=1
    g55: Circle CenterX=236.821 CenterY=-24.2775 CenterZ=0 NormalX=0 NormalY=0 NormalZ=1 AngleXU=0 Radius=1
    g56: BSplineCurve PolesCount=3 KnotsCount=2 Degree=2 IsPeriodic=0
    g57: GeomPoint X=238.538 Y=-21.7539 Z=0
    g58: GeomPoint X=236.821 Y=-24.2775 Z=0
    g59: Circle CenterX=125.607 CenterY=-21.7539 CenterZ=0 NormalX=0 NormalY=0 NormalZ=1 AngleXU=0 Radius=1
    g60: Circle CenterX=139.632 CenterY=-14.0532 CenterZ=0 NormalX=0 NormalY=0 NormalZ=1 AngleXU=0 Radius=1
    g61: Circle CenterX=127.325 CenterY=-24.2775 CenterZ=0 NormalX=0 NormalY=0 NormalZ=1 AngleXU=0 Radius=1
    g62: BSplineCurve PolesCount=3 KnotsCount=2 Degree=2 IsPeriodic=0
    g63: GeomPoint X=125.607 Y=-21.7539 Z=0
    g64: GeomPoint X=127.325 Y=-24.2775 Z=0
    g65: Circle CenterX=302.996 CenterY=111.695 CenterZ=0 NormalX=0 NormalY=0 NormalZ=1 AngleXU=0 Radius=1
    g66: Circle CenterX=306.073 CenterY=114.251 CenterZ=0 NormalX=0 NormalY=0 NormalZ=1 AngleXU=0 Radius=1
    g67: Circle CenterX=306.073 CenterY=110.251 CenterZ=0 NormalX=0 NormalY=0 NormalZ=1 AngleXU=0 Radius=1
    g68: BSplineCurve PolesCount=3 KnotsCount=2 Degree=2 IsPeriodic=0
    g69: GeomPoint X=302.996 Y=111.695 Z=0
    g70: GeomPoint X=306.073 Y=110.251 Z=0
    g71: Circle CenterX=306.073 CenterY=95.2763 CenterZ=0 NormalX=0 NormalY=0 NormalZ=1 AngleXU=0 Radius=1
    g72: Circle CenterX=306.073 CenterY=91.2763 CenterZ=0 NormalX=0 NormalY=0 NormalZ=1 AngleXU=0 Radius=1
    g73: Circle CenterX=302.567 CenterY=89.3511 CenterZ=0 NormalX=0 NormalY=0 NormalZ=1 AngleXU=0 Radius=1
    g74: BSplineCurve PolesCount=3 KnotsCount=2 Degree=2 IsPeriodic=0
    g75: GeomPoint X=306.073 Y=95.2763 Z=0
    g76: GeomPoint X=302.567 Y=89.3511 Z=0
    g77: LineSegment StartX=306.073 StartY=110.251 StartZ=0 EndX=306.073 EndY=95.2763 EndZ=0
    g78: LineSegment StartX=302.996 StartY=111.695 StartZ=0 EndX=236.821 EndY=56.7187 EndZ=0
    g79: LineSegment StartX=238.538 StartY=54.1951 StartZ=0 EndX=302.567 EndY=89.3511 EndZ=0
    g80: Circle CenterX=61.1496 CenterY=111.695 CenterZ=0 NormalX=0 NormalY=0 NormalZ=1 AngleXU=0 Radius=1
    g81: Circle CenterX=58.0728 CenterY=114.251 CenterZ=0 NormalX=0 NormalY=0 NormalZ=1 AngleXU=0 Radius=1
    g82: Circle CenterX=58.0728 CenterY=110.251 CenterZ=0 NormalX=0 NormalY=0 NormalZ=1 AngleXU=0 Radius=1
    g83: BSplineCurve PolesCount=3 KnotsCount=2 Degree=2 IsPeriodic=0
    g84: GeomPoint X=61.1496 Y=111.695 Z=0
    g85: GeomPoint X=58.0728 Y=110.251 Z=0
    g86: Circle CenterX=61.5791 CenterY=89.3511 CenterZ=0 NormalX=0 NormalY=0 NormalZ=1 AngleXU=0 Radius=1
    g87: Circle CenterX=58.0728 CenterY=91.2763 CenterZ=0 NormalX=0 NormalY=0 NormalZ=1 AngleXU=0 Radius=1
    g88: Circle CenterX=58.0728 CenterY=95.2763 CenterZ=0 NormalX=0 NormalY=0 NormalZ=1 AngleXU=0 Radius=1
    g89: BSplineCurve PolesCount=3 KnotsCount=2 Degree=2 IsPeriodic=0
    g90: GeomPoint X=61.5791 Y=89.3511 Z=0
    g91: GeomPoint X=58.0728 Y=95.2763 Z=0
    g92: LineSegment StartX=58.0728 StartY=110.251 StartZ=0 EndX=58.0728 EndY=95.2763 EndZ=0
    g93: LineSegment StartX=61.1496 StartY=111.695 StartZ=0 EndX=127.326 EndY=56.7187 EndZ=0
    g94: LineSegment StartX=125.607 StartY=54.1951 StartZ=0 EndX=61.5791 EndY=89.3511 EndZ=0
    g95: Circle CenterX=61.5791 CenterY=-56.9099 CenterZ=0 NormalX=0 NormalY=0 NormalZ=1 AngleXU=0 Radius=1
    g96: Circle CenterX=58.0728 CenterY=-58.8351 CenterZ=0 NormalX=0 NormalY=0 NormalZ=1 AngleXU=0 Radius=1
    g97: Circle CenterX=58.0728 CenterY=-62.8351 CenterZ=0 NormalX=0 NormalY=0 NormalZ=1 AngleXU=0 Radius=1
    g98: BSplineCurve PolesCount=3 KnotsCount=2 Degree=2 IsPeriodic=0
    g99: GeomPoint X=61.5791 Y=-56.9099 Z=0
    g100: GeomPoint X=58.0728 Y=-62.8351 Z=0
    g101: Circle CenterX=58.0728 CenterY=-77.8102 CenterZ=0 NormalX=0 NormalY=0 NormalZ=1 AngleXU=0 Radius=1
    g102: Circle CenterX=58.0728 CenterY=-81.8102 CenterZ=0 NormalX=0 NormalY=0 NormalZ=1 AngleXU=0 Radius=1
    g103: Circle CenterX=61.1496 CenterY=-79.2541 CenterZ=0 NormalX=0 NormalY=0 NormalZ=1 AngleXU=0 Radius=1
    g104: BSplineCurve PolesCount=3 KnotsCount=2 Degree=2 IsPeriodic=0
    g105: GeomPoint X=58.0728 Y=-77.8102 Z=0
    g106: GeomPoint X=61.1496 Y=-79.2541 Z=0
    g107: LineSegment StartX=58.0728 StartY=-62.8351 StartZ=0 EndX=58.0728 EndY=-77.8102 EndZ=0
    g108: LineSegment StartX=61.1496 StartY=-79.2541 StartZ=0 EndX=127.325 EndY=-24.2775 EndZ=0
    g109: LineSegment StartX=125.607 StartY=-21.7539 StartZ=0 EndX=61.5791 EndY=-56.9099 EndZ=0
    g110: Circle CenterX=302.567 CenterY=-56.9099 CenterZ=0 NormalX=0 NormalY=0 NormalZ=1 AngleXU=0 Radius=1
    g111: Circle CenterX=306.073 CenterY=-58.8351 CenterZ=0 NormalX=0 NormalY=0 NormalZ=1 AngleXU=0 Radius=1
    g112: Circle CenterX=306.073 CenterY=-62.8351 CenterZ=0 NormalX=0 NormalY=0 NormalZ=1 AngleXU=0 Radius=1
    g113: BSplineCurve PolesCount=3 KnotsCount=2 Degree=2 IsPeriodic=0
    g114: GeomPoint X=302.567 Y=-56.9099 Z=0
    g115: GeomPoint X=306.073 Y=-62.8351 Z=0
    g116: Circle CenterX=302.996 CenterY=-79.2541 CenterZ=0 NormalX=0 NormalY=0 NormalZ=1 AngleXU=0 Radius=1
    g117: Circle CenterX=306.073 CenterY=-81.8102 CenterZ=0 NormalX=0 NormalY=0 NormalZ=1 AngleXU=0 Radius=1
    g118: Circle CenterX=306.073 CenterY=-77.8102 CenterZ=0 NormalX=0 NormalY=0 NormalZ=1 AngleXU=0 Radius=1
    g119: BSplineCurve PolesCount=3 KnotsCount=2 Degree=2 IsPeriodic=0
    g120: GeomPoint X=302.996 Y=-79.2541 Z=0
    g121: GeomPoint X=306.073 Y=-77.8102 Z=0
    g122: LineSegment StartX=306.073 StartY=-62.8351 StartZ=0 EndX=306.073 EndY=-77.8102 EndZ=0
    g123: LineSegment StartX=302.996 StartY=-79.2541 StartZ=0 EndX=236.821 EndY=-24.2775 EndZ=0
    g124: LineSegment StartX=238.538 StartY=-21.7539 StartZ=0 EndX=302.567 EndY=-56.9099 EndZ=0
    g125: Circle CenterX=61.6457 CenterY=-88.8112 CenterZ=0 NormalX=0 NormalY=0 NormalZ=1 AngleXU=0 Radius=1
    g126: Circle CenterX=58.0728 CenterY=-91.7794 CenterZ=0 NormalX=0 NormalY=0 NormalZ=1 AngleXU=0 Radius=1
    g127: Circle CenterX=63.9135 CenterY=-91.7794 CenterZ=0 NormalX=0 NormalY=0 NormalZ=1 AngleXU=0 Radius=1
    g128: BSplineCurve PolesCount=3 KnotsCount=2 Degree=2 IsPeriodic=0
    g129: GeomPoint X=61.6457 Y=-88.8112 Z=0
    g130: GeomPoint X=63.9135 Y=-91.7794 Z=0
    g131: Circle CenterX=179.022 CenterY=-85.8163 CenterZ=0 NormalX=0 NormalY=0 NormalZ=1 AngleXU=0 Radius=1
    g132: Circle CenterX=179.022 CenterY=-91.7794 CenterZ=0 NormalX=0 NormalY=0 NormalZ=1 AngleXU=0 Radius=1
    g133: Circle CenterX=171.895 CenterY=-91.7794 CenterZ=0 NormalX=0 NormalY=0 NormalZ=1 AngleXU=0 Radius=1
    g134: BSplineCurve PolesCount=3 KnotsCount=2 Degree=2 IsPeriodic=0
    g135: GeomPoint X=179.022 Y=-85.8163 Z=0
    g136: GeomPoint X=171.895 Y=-91.7794 Z=0
    g137: Circle CenterX=185.124 CenterY=-86.2028 CenterZ=0 NormalX=0 NormalY=0 NormalZ=1 AngleXU=0 Radius=1
    g138: Circle CenterX=185.124 CenterY=-91.7794 CenterZ=0 NormalX=0 NormalY=0 NormalZ=1 AngleXU=0 Radius=1
    g139: Circle CenterX=191.747 CenterY=-91.7794 CenterZ=0 NormalX=0 NormalY=0 NormalZ=1 AngleXU=0 Radius=1
    g140: BSplineCurve PolesCount=3 KnotsCount=2 Degree=2 IsPeriodic=0
    g141: GeomPoint X=185.124 Y=-86.2028 Z=0
    g142: GeomPoint X=191.747 Y=-91.7794 Z=0
    g143: Circle CenterX=299.888 CenterY=-86.6413 CenterZ=0 NormalX=0 NormalY=0 NormalZ=1 AngleXU=0 Radius=1
    g144: Circle CenterX=306.073 CenterY=-91.7794 CenterZ=0 NormalX=0 NormalY=0 NormalZ=1 AngleXU=0 Radius=1
    g145: Circle CenterX=298.776 CenterY=-91.7794 CenterZ=0 NormalX=0 NormalY=0 NormalZ=1 AngleXU=0 Radius=1
    g146: BSplineCurve PolesCount=3 KnotsCount=2 Degree=2 IsPeriodic=0
    g147: GeomPoint X=299.888 Y=-86.6413 Z=0
    g148: GeomPoint X=298.776 Y=-91.7794 Z=0
    g149: LineSegment StartX=189.124 StartY=5.37834 StartZ=0 EndX=299.888 EndY=-86.6413 EndZ=0
    g150: LineSegment StartX=298.776 StartY=-91.7794 StartZ=0 EndX=191.747 EndY=-91.7794 EndZ=0
    g151: LineSegment StartX=185.124 StartY=-86.2028 StartZ=0 EndX=185.124 EndY=5.34704 EndZ=0
    g152: LineSegment StartX=179.022 StartY=5.34704 StartZ=0 EndX=179.022 EndY=-85.8163 EndZ=0
    g153: LineSegment StartX=171.895 StartY=-91.7794 StartZ=0 EndX=63.9135 EndY=-91.7794 EndZ=0
    g154: LineSegment StartX=61.6457 StartY=-88.8112 StartZ=0 EndX=175.022 EndY=5.37834 EndZ=0
    g155: Circle CenterX=302.073 CenterY=124.221 CenterZ=0 NormalX=0 NormalY=0 NormalZ=1 AngleXU=0 Radius=1
    g156: Circle CenterX=306.073 CenterY=124.221 CenterZ=0 NormalX=0 NormalY=0 NormalZ=1 AngleXU=0 Radius=1
    g157: Circle CenterX=302.996 CenterY=121.665 CenterZ=0 NormalX=0 NormalY=0 NormalZ=1 AngleXU=0 Radius=1
    g158: BSplineCurve PolesCount=3 KnotsCount=2 Degree=2 IsPeriodic=0
    g159: GeomPoint X=302.073 Y=124.221 Z=0
    g160: GeomPoint X=302.996 Y=121.665 Z=0
    g161: Circle CenterX=189.124 CenterY=124.221 CenterZ=0 NormalX=0 NormalY=0 NormalZ=1 AngleXU=0 Radius=1
    g162: Circle CenterX=185.124 CenterY=124.221 CenterZ=0 NormalX=0 NormalY=0 NormalZ=1 AngleXU=0 Radius=1
    g163: Circle CenterX=185.124 CenterY=120.221 CenterZ=0 NormalX=0 NormalY=0 NormalZ=1 AngleXU=0 Radius=1
    g164: BSplineCurve PolesCount=3 KnotsCount=2 Degree=2 IsPeriodic=0
    g165: GeomPoint X=189.124 Y=124.221 Z=0
    g166: GeomPoint X=185.124 Y=120.221 Z=0
    g167: Circle CenterX=175.022 CenterY=124.221 CenterZ=0 NormalX=0 NormalY=0 NormalZ=1 AngleXU=0 Radius=1
    g168: Circle CenterX=179.022 CenterY=124.221 CenterZ=0 NormalX=0 NormalY=0 NormalZ=1 AngleXU=0 Radius=1
    g169: Circle CenterX=179.022 CenterY=120.221 CenterZ=0 NormalX=0 NormalY=0 NormalZ=1 AngleXU=0 Radius=1
    g170: BSplineCurve PolesCount=3 KnotsCount=2 Degree=2 IsPeriodic=0
    g171: GeomPoint X=175.022 Y=124.221 Z=0
    g172: GeomPoint X=179.022 Y=120.221 Z=0
    g173: Circle CenterX=62.0728 CenterY=124.221 CenterZ=0 NormalX=0 NormalY=0 NormalZ=1 AngleXU=0 Radius=1
    g174: Circle CenterX=58.0728 CenterY=124.221 CenterZ=0 NormalX=0 NormalY=0 NormalZ=1 AngleXU=0 Radius=1
    g175: Circle CenterX=61.1496 CenterY=121.665 CenterZ=0 NormalX=0 NormalY=0 NormalZ=1 AngleXU=0 Radius=1
    g176: BSplineCurve PolesCount=3 KnotsCount=2 Degree=2 IsPeriodic=0
    g177: GeomPoint X=62.0728 Y=124.221 Z=0
    g178: GeomPoint X=61.1496 Y=121.665 Z=0
    g179: LineSegment StartX=179.022 StartY=120.221 StartZ=0 EndX=179.022 EndY=27.0628 EndZ=0
    g180: LineSegment StartX=185.124 StartY=27.0628 StartZ=0 EndX=185.124 EndY=120.221 EndZ=0
    g181: LineSegment StartX=302.996 StartY=121.665 StartZ=0 EndX=189.124 EndY=27.0628 EndZ=0
    g182: LineSegment StartX=175.022 StartY=27.0628 StartZ=0 EndX=61.1496 EndY=121.665 EndZ=0
    g183: Circle CenterX=61.5791 CenterY=75.4095 CenterZ=0 NormalX=0 NormalY=0 NormalZ=1 AngleXU=0 Radius=1
    g184: Circle CenterX=58.0728 CenterY=77.3346 CenterZ=0 NormalX=0 NormalY=0 NormalZ=1 AngleXU=0 Radius=1
    g185: Circle CenterX=58.0728 CenterY=73.3346 CenterZ=0 NormalX=0 NormalY=0 NormalZ=1 AngleXU=0 Radius=1
    g186: BSplineCurve PolesCount=3 KnotsCount=2 Degree=2 IsPeriodic=0
    g187: GeomPoint X=61.5791 Y=75.4095 Z=0
    g188: GeomPoint X=58.0728 Y=73.3346 Z=0
    g189: Circle CenterX=58.0728 CenterY=-40.8935 CenterZ=0 NormalX=0 NormalY=0 NormalZ=1 AngleXU=0 Radius=1
    g190: Circle CenterX=58.0728 CenterY=-44.8935 CenterZ=0 NormalX=0 NormalY=0 NormalZ=1 AngleXU=0 Radius=1
    g191: Circle CenterX=61.5791 CenterY=-42.9683 CenterZ=0 NormalX=0 NormalY=0 NormalZ=1 AngleXU=0 Radius=1
    g192: BSplineCurve PolesCount=3 KnotsCount=2 Degree=2 IsPeriodic=0
    g193: GeomPoint X=58.0728 Y=-40.8935 Z=0
    g194: GeomPoint X=61.5791 Y=-42.9683 Z=0
    g195: LineSegment StartX=61.5791 StartY=-42.9683 StartZ=0 EndX=165.871 EndY=14.2954 EndZ=0
    g196: LineSegment StartX=165.871 StartY=18.1458 StartZ=0 EndX=61.5791 EndY=75.4095 EndZ=0
    g197: LineSegment StartX=58.0728 StartY=73.3346 StartZ=0 EndX=58.0728 EndY=-40.8935 EndZ=0
    g198: Circle CenterX=302.567 CenterY=-42.9683 CenterZ=0 NormalX=0 NormalY=0 NormalZ=1 AngleXU=0 Radius=1
    g199: Circle CenterX=306.073 CenterY=-44.8935 CenterZ=0 NormalX=0 NormalY=0 NormalZ=1 AngleXU=0 Radius=1
    g200: Circle CenterX=306.073 CenterY=-40.8935 CenterZ=0 NormalX=0 NormalY=0 NormalZ=1 AngleXU=0 Radius=1
    g201: BSplineCurve PolesCount=3 KnotsCount=2 Degree=2 IsPeriodic=0
    g202: GeomPoint X=302.567 Y=-42.9683 Z=0
    g203: GeomPoint X=306.073 Y=-40.8935 Z=0
    g204: Circle CenterX=306.073 CenterY=73.3346 CenterZ=0 NormalX=0 NormalY=0 NormalZ=1 AngleXU=0 Radius=1
    g205: Circle CenterX=306.073 CenterY=77.3346 CenterZ=0 NormalX=0 NormalY=0 NormalZ=1 AngleXU=0 Radius=1
    g206: Circle CenterX=302.567 CenterY=75.4095 CenterZ=0 NormalX=0 NormalY=0 NormalZ=1 AngleXU=0 Radius=1
    g207: BSplineCurve PolesCount=3 KnotsCount=2 Degree=2 IsPeriodic=0
    g208: GeomPoint X=306.073 Y=73.3346 Z=0
    g209: GeomPoint X=302.567 Y=75.4095 Z=0
    g210: LineSegment StartX=302.567 StartY=-42.9683 StartZ=0 EndX=198.275 EndY=14.2954 EndZ=0
    g211: LineSegment StartX=198.275 StartY=18.1458 StartZ=0 EndX=302.567 EndY=75.4095 EndZ=0
    g212: LineSegment StartX=306.073 StartY=73.3346 StartZ=0 EndX=306.073 EndY=-40.8935 EndZ=0
    g213: LineSegment StartX=322.073 StartY=105.865 StartZ=0 EndX=328.643 EndY=105.865 EndZ=0
    g214: LineSegment StartX=318.073 StartY=120.221 StartZ=0 EndX=318.073 EndY=109.865 EndZ=0
    g215: LineSegment StartX=336.157 StartY=107.779 StartZ=0 EndX=362.567 EndY=122.294 EndZ=0
    g216: Circle CenterX=362.073 CenterY=124.221 CenterZ=0 NormalX=0 NormalY=0 NormalZ=1 AngleXU=0 Radius=1
    g217: Circle CenterX=366.073 CenterY=124.221 CenterZ=0 NormalX=0 NormalY=0 NormalZ=1 AngleXU=0 Radius=1
    g218: Circle CenterX=362.567 CenterY=122.294 CenterZ=0 NormalX=0 NormalY=0 NormalZ=1 AngleXU=0 Radius=1
    g219: BSplineCurve PolesCount=3 KnotsCount=2 Degree=2 IsPeriodic=0
    g220: GeomPoint X=362.073 Y=124.221 Z=0
    g221: GeomPoint X=362.567 Y=122.294 Z=0
    g222: Circle CenterX=322.073 CenterY=124.221 CenterZ=0 NormalX=0 NormalY=0 NormalZ=1 AngleXU=0 Radius=1
    g223: Circle CenterX=318.073 CenterY=124.221 CenterZ=0 NormalX=0 NormalY=0 NormalZ=1 AngleXU=0 Radius=1
    g224: Circle CenterX=318.073 CenterY=120.221 CenterZ=0 NormalX=0 NormalY=0 NormalZ=1 AngleXU=0 Radius=1
    g225: BSplineCurve PolesCount=3 KnotsCount=2 Degree=2 IsPeriodic=0
    g226: GeomPoint X=322.073 Y=124.221 Z=0
    g227: GeomPoint X=318.073 Y=120.221 Z=0
    g228: Circle CenterX=322.073 CenterY=105.865 CenterZ=0 NormalX=0 NormalY=0 NormalZ=1 AngleXU=0 Radius=1
    g229: Circle CenterX=318.073 CenterY=105.865 CenterZ=0 NormalX=0 NormalY=0 NormalZ=1 AngleXU=0 Radius=1
    g230: Circle CenterX=318.073 CenterY=109.865 CenterZ=0 NormalX=0 NormalY=0 NormalZ=1 AngleXU=0 Radius=1
    g231: BSplineCurve PolesCount=3 KnotsCount=2 Degree=2 IsPeriodic=0
    g232: GeomPoint X=322.073 Y=105.865 Z=0
    g233: GeomPoint X=318.073 Y=109.865 Z=0
    g234: Circle CenterX=336.157 CenterY=107.779 CenterZ=0 NormalX=0 NormalY=0 NormalZ=1 AngleXU=0 Radius=1
    g235: Circle CenterX=332.651 CenterY=105.853 CenterZ=0 NormalX=0 NormalY=0 NormalZ=1 AngleXU=0 Radius=1
    g236: Circle CenterX=328.643 CenterY=105.865 CenterZ=0 NormalX=0 NormalY=0 NormalZ=1 AngleXU=0 Radius=1
    g237: BSplineCurve PolesCount=3 KnotsCount=2 Degree=2 IsPeriodic=0
    g238: GeomPoint X=336.157 Y=107.779 Z=0
    g239: GeomPoint X=328.643 Y=105.865 Z=0
    g240: LineSegment StartX=322.073 StartY=124.221 StartZ=0 EndX=362.073 EndY=124.221 EndZ=0
    g241: Circle CenterX=371.567 CenterY=-80.8644 CenterZ=0 NormalX=0 NormalY=0 NormalZ=1 AngleXU=0 Radius=1
    g242: Circle CenterX=375.073 CenterY=-82.7896 CenterZ=0 NormalX=0 NormalY=0 NormalZ=1 AngleXU=0 Radius=1
    g243: Circle CenterX=375.073 CenterY=-78.7896 CenterZ=0 NormalX=0 NormalY=0 NormalZ=1 AngleXU=0 Radius=1
    g244: BSplineCurve PolesCount=3 KnotsCount=2 Degree=2 IsPeriodic=0
    g245: GeomPoint X=371.567 Y=-80.8644 Z=0
    g246: GeomPoint X=375.073 Y=-78.7896 Z=0
    g247: Circle CenterX=321.579 CenterY=-53.4075 CenterZ=0 NormalX=0 NormalY=0 NormalZ=1 AngleXU=0 Radius=1
    g248: Circle CenterX=318.073 CenterY=-51.4823 CenterZ=0 NormalX=0 NormalY=0 NormalZ=1 AngleXU=0 Radius=1
    g249: Circle CenterX=318.073 CenterY=-47.4805 CenterZ=0 NormalX=0 NormalY=0 NormalZ=1 AngleXU=0 Radius=1
    g250: BSplineCurve PolesCount=3 KnotsCount=2 Degree=2 IsPeriodic=0
    g251: GeomPoint X=321.579 Y=-53.4075 Z=0
    g252: GeomPoint X=318.073 Y=-47.4805 Z=0
    g253: LineSegment StartX=371.567 StartY=-80.8644 StartZ=0 EndX=321.579 EndY=-53.4075 EndZ=0
    g254: Circle CenterX=321.579 CenterY=-67.3492 CenterZ=0 NormalX=0 NormalY=0 NormalZ=1 AngleXU=0 Radius=1
    g255: Circle CenterX=318.073 CenterY=-65.424 CenterZ=0 NormalX=0 NormalY=0 NormalZ=1 AngleXU=0 Radius=1
    g256: Circle CenterX=318.073 CenterY=-69.424 CenterZ=0 NormalX=0 NormalY=0 NormalZ=1 AngleXU=0 Radius=1
    g257: BSplineCurve PolesCount=3 KnotsCount=2 Degree=2 IsPeriodic=0
    g258: GeomPoint X=321.579 Y=-67.3492 Z=0
    g259: GeomPoint X=318.073 Y=-69.424 Z=0
    g260: Circle CenterX=362.567 CenterY=-89.8542 CenterZ=0 NormalX=0 NormalY=0 NormalZ=1 AngleXU=0 Radius=1
    g261: Circle CenterX=366.073 CenterY=-91.7794 CenterZ=0 NormalX=0 NormalY=0 NormalZ=1 AngleXU=0 Radius=1
    g262: Circle CenterX=362.073 CenterY=-91.7794 CenterZ=0 NormalX=0 NormalY=0 NormalZ=1 AngleXU=0 Radius=1
    g263: BSplineCurve PolesCount=3 KnotsCount=2 Degree=2 IsPeriodic=0
    g264: GeomPoint X=362.567 Y=-89.8542 Z=0
    g265: GeomPoint X=362.073 Y=-91.7794 Z=0
    g266: Circle CenterX=322.073 CenterY=-91.7794 CenterZ=0 NormalX=0 NormalY=0 NormalZ=1 AngleXU=0 Radius=1
    g267: Circle CenterX=318.073 CenterY=-91.7794 CenterZ=0 NormalX=0 NormalY=0 NormalZ=1 AngleXU=0 Radius=1
    g268: Circle CenterX=318.073 CenterY=-87.7794 CenterZ=0 NormalX=0 NormalY=0 NormalZ=1 AngleXU=0 Radius=1
    g269: BSplineCurve PolesCount=3 KnotsCount=2 Degree=2 IsPeriodic=0
    g270: GeomPoint X=322.073 Y=-91.7794 Z=0
    g271: GeomPoint X=318.073 Y=-87.7794 Z=0
    g272: LineSegment StartX=362.567 StartY=-89.8542 StartZ=0 EndX=321.579 EndY=-67.3492 EndZ=0
    g273: LineSegment StartX=318.073 StartY=-69.424 StartZ=0 EndX=318.073 EndY=-87.7794 EndZ=0
    g274: LineSegment StartX=322.073 StartY=-91.7794 StartZ=0 EndX=362.073 EndY=-91.7794 EndZ=0
    g275: Circle CenterX=2.07281 CenterY=124.221 CenterZ=0 NormalX=0 NormalY=0 NormalZ=1 AngleXU=0 Radius=1
    g276: Circle CenterX=1.57905 CenterY=122.295 CenterZ=0 NormalX=0 NormalY=0 NormalZ=1 AngleXU=0 Radius=1
    g277: BSplineCurve PolesCount=3 KnotsCount=2 Degree=2 IsPeriodic=0
    g278: GeomPoint X=2.07281 Y=124.221 Z=0
    g279: GeomPoint X=1.57905 Y=122.295 Z=0
    g280: Circle CenterX=42.0728 CenterY=124.221 CenterZ=0 NormalX=0 NormalY=0 NormalZ=1 AngleXU=0 Radius=1
    g281: Circle CenterX=46.0728 CenterY=124.221 CenterZ=0 NormalX=0 NormalY=0 NormalZ=1 AngleXU=0 Radius=1
    g282: Circle CenterX=46.0728 CenterY=120.221 CenterZ=0 NormalX=0 NormalY=0 NormalZ=1 AngleXU=0 Radius=1
    g283: BSplineCurve PolesCount=3 KnotsCount=2 Degree=2 IsPeriodic=0
    g284: GeomPoint X=42.0728 Y=124.221 Z=0
    g285: GeomPoint X=46.0728 Y=120.221 Z=0
    g286: Circle CenterX=46.0728 CenterY=109.865 CenterZ=0 NormalX=0 NormalY=0 NormalZ=1 AngleXU=0 Radius=1
    g287: Circle CenterX=46.0728 CenterY=105.865 CenterZ=0 NormalX=0 NormalY=0 NormalZ=1 AngleXU=0 Radius=1
    g288: Circle CenterX=42.0728 CenterY=105.865 CenterZ=0 NormalX=0 NormalY=0 NormalZ=1 AngleXU=0 Radius=1
    g289: BSplineCurve PolesCount=3 KnotsCount=2 Degree=2 IsPeriodic=0
    g290: GeomPoint X=46.0728 Y=109.865 Z=0
    g291: GeomPoint X=42.0728 Y=105.865 Z=0
    g292: Circle CenterX=35.5028 CenterY=105.865 CenterZ=0 NormalX=0 NormalY=0 NormalZ=1 AngleXU=0 Radius=1
    g293: Circle CenterX=31.5028 CenterY=105.865 CenterZ=0 NormalX=0 NormalY=0 NormalZ=1 AngleXU=0 Radius=1
    g294: Circle CenterX=27.9965 CenterY=107.79 CenterZ=0 NormalX=0 NormalY=0 NormalZ=1 AngleXU=0 Radius=1
    g295: BSplineCurve PolesCount=3 KnotsCount=2 Degree=2 IsPeriodic=0
    g296: GeomPoint X=35.5028 Y=105.865 Z=0
    g297: GeomPoint X=27.9965 Y=107.79 Z=0
    g298: LineSegment StartX=2.07281 StartY=124.221 StartZ=0 EndX=42.0728 EndY=124.221 EndZ=0
    g299: LineSegment StartX=46.0728 StartY=120.221 StartZ=0 EndX=46.0728 EndY=109.865 EndZ=0
    g300: LineSegment StartX=42.0728 StartY=105.865 StartZ=0 EndX=35.5028 EndY=105.865 EndZ=0
    g301: LineSegment StartX=27.9965 StartY=107.79 StartZ=0 EndX=1.57905 EndY=122.295 EndZ=0
    g302: Circle CenterX=42.5666 CenterY=-67.3492 CenterZ=0 NormalX=0 NormalY=0 NormalZ=1 AngleXU=0 Radius=1
    g303: Circle CenterX=46.0728 CenterY=-65.424 CenterZ=0 NormalX=0 NormalY=0 NormalZ=1 AngleXU=0 Radius=1
    g304: Circle CenterX=46.0728 CenterY=-69.424 CenterZ=0 NormalX=0 NormalY=0 NormalZ=1 AngleXU=0 Radius=1
    g305: BSplineCurve PolesCount=3 KnotsCount=2 Degree=2 IsPeriodic=0
    g306: GeomPoint X=42.5666 Y=-67.3492 Z=0
    g307: GeomPoint X=46.0728 Y=-69.424 Z=0
    g308: Circle CenterX=46.0728 CenterY=-87.7794 CenterZ=0 NormalX=0 NormalY=0 NormalZ=1 AngleXU=0 Radius=1
    g309: Circle CenterX=46.0728 CenterY=-91.7794 CenterZ=0 NormalX=0 NormalY=0 NormalZ=1 AngleXU=0 Radius=1
    g310: Circle CenterX=42.0728 CenterY=-91.7794 CenterZ=0 NormalX=0 NormalY=0 NormalZ=1 AngleXU=0 Radius=1
    g311: BSplineCurve PolesCount=3 KnotsCount=2 Degree=2 IsPeriodic=0
    g312: GeomPoint X=46.0728 Y=-87.7794 Z=0
    g313: GeomPoint X=42.0728 Y=-91.7794 Z=0
    g314: Circle CenterX=2.07281 CenterY=-91.7794 CenterZ=0 NormalX=0 NormalY=0 NormalZ=1 AngleXU=0 Radius=1
    g315: Circle CenterX=-1.92719 CenterY=-91.7794 CenterZ=0 NormalX=0 NormalY=0 NormalZ=1 AngleXU=0 Radius=1
    g316: Circle CenterX=1.57905 CenterY=-89.8542 CenterZ=0 NormalX=0 NormalY=0 NormalZ=1 AngleXU=0 Radius=1
    g317: BSplineCurve PolesCount=3 KnotsCount=2 Degree=2 IsPeriodic=0
    g318: GeomPoint X=2.07281 Y=-91.7794 Z=0
    g319: GeomPoint X=1.57905 Y=-89.8542 Z=0
    g320: LineSegment StartX=2.07281 StartY=-91.7794 StartZ=0 EndX=42.0728 EndY=-91.7794 EndZ=0
    g321: LineSegment StartX=46.0728 StartY=-87.7794 StartZ=0 EndX=46.0728 EndY=-69.424 EndZ=0
    g322: LineSegment StartX=42.5666 StartY=-67.3492 StartZ=0 EndX=1.57905 EndY=-89.8542 EndZ=0
    g323: Circle CenterX=322.073 CenterY=76.4095 CenterZ=0 NormalX=0 NormalY=0 NormalZ=1 AngleXU=0 Radius=4
    g324: BSplineCurve PolesCount=3 KnotsCount=2 Degree=2 IsPeriodic=0
    g325: GeomPoint X=318.073 Y=72.4095 Z=0
    g326: GeomPoint X=322.073 Y=76.4095 Z=0
    g327: Circle CenterX=375.073 CenterY=72.4095 CenterZ=0 NormalX=0 NormalY=0 NormalZ=1 AngleXU=0 Radius=1
    g328: Circle CenterX=375.073 CenterY=76.4095 CenterZ=0 NormalX=0 NormalY=0 NormalZ=1 AngleXU=0 Radius=1
    g329: Circle CenterX=371.073 CenterY=76.4095 CenterZ=0 NormalX=0 NormalY=0 NormalZ=1 AngleXU=0 Radius=1
    g330: BSplineCurve PolesCount=3 KnotsCount=2 Degree=2 IsPeriodic=0
    g331: GeomPoint X=375.073 Y=72.4095 Z=0
    g332: GeomPoint X=371.073 Y=76.4095 Z=0
    g333: LineSegment StartX=322.073 StartY=76.4095 StartZ=0 EndX=371.073 EndY=76.4095 EndZ=0
    g334: LineSegment StartX=318.073 StartY=72.4095 StartZ=0 EndX=318.073 EndY=-47.4805 EndZ=0
    g335: LineSegment StartX=375.073 StartY=72.4095 StartZ=0 EndX=375.073 EndY=-78.7896 EndZ=0
    g336: ArcOfCircle CenterX=-26.9272 CenterY=22.1087 CenterZ=0 NormalX=0 NormalY=0 NormalZ=1 AngleXU=0 Radius=4 StartAngle=5e-16 EndAngle=3.14159
    g337: LineSegment StartX=-22.9272 StartY=22.1087 StartZ=0 EndX=-18.9272 EndY=-83.7794 EndZ=0
    g338: LineSegment StartX=-34.9272 StartY=-83.7794 StartZ=0 EndX=-30.9272 EndY=22.1087 EndZ=0
    g339: ArcOfCircle CenterX=391.073 CenterY=22.1087 CenterZ=0 NormalX=0 NormalY=0 NormalZ=1 AngleXU=0 Radius=4 StartAngle=0 EndAngle=3.14159
    g340: LineSegment StartX=387.073 StartY=22.1087 StartZ=0 EndX=383.073 EndY=-83.7794 EndZ=0
    g341: LineSegment StartX=395.073 StartY=22.1087 StartZ=0 EndX=399.073 EndY=-83.7794 EndZ=0
    g342: Circle CenterX=-10.9272 CenterY=-78.7794 CenterZ=0 NormalX=0 NormalY=0 NormalZ=1 AngleXU=0 Radius=1
    g343: Circle CenterX=-10.9272 CenterY=-82.7794 CenterZ=0 NormalX=0 NormalY=0 NormalZ=1 AngleXU=0 Radius=1
    g344: Circle CenterX=-7.42095 CenterY=-80.8542 CenterZ=0 NormalX=0 NormalY=0 NormalZ=1 AngleXU=0 Radius=1
    g345: BSplineCurve PolesCount=3 KnotsCount=2 Degree=2 IsPeriodic=0
    g346: GeomPoint X=-10.9272 Y=-78.7794 Z=0
    g347: GeomPoint X=-7.42095 Y=-80.8542 Z=0
    g348: Circle CenterX=42.5666 CenterY=-53.4075 CenterZ=0 NormalX=0 NormalY=0 NormalZ=1 AngleXU=0 Radius=1
    g349: Circle CenterX=46.0728 CenterY=-51.4823 CenterZ=0 NormalX=0 NormalY=0 NormalZ=1 AngleXU=0 Radius=1
    g350: Circle CenterX=46.0728 CenterY=-47.4823 CenterZ=0 NormalX=0 NormalY=0 NormalZ=1 AngleXU=0 Radius=1
    g351: BSplineCurve PolesCount=3 KnotsCount=2 Degree=2 IsPeriodic=0
    g352: GeomPoint X=42.5666 Y=-53.4075 Z=0
    g353: GeomPoint X=46.0728 Y=-47.4823 Z=0
    g354: Circle CenterX=46.0728 CenterY=72.4095 CenterZ=0 NormalX=0 NormalY=0 NormalZ=1 AngleXU=0 Radius=1
    g355: Circle CenterX=46.0728 CenterY=76.4095 CenterZ=0 NormalX=0 NormalY=0 NormalZ=1 AngleXU=0 Radius=1
    g356: Circle CenterX=42.0728 CenterY=76.4095 CenterZ=0 NormalX=0 NormalY=0 NormalZ=1 AngleXU=0 Radius=1
    g357: BSplineCurve PolesCount=3 KnotsCount=2 Degree=2 IsPeriodic=0
    g358: GeomPoint X=46.0728 Y=72.4095 Z=0
    g359: GeomPoint X=42.0728 Y=76.4095 Z=0
    g360: Circle CenterX=-6.92718 CenterY=76.4095 CenterZ=0 NormalX=0 NormalY=0 NormalZ=1 AngleXU=0 Radius=1
    g361: Circle CenterX=-10.9272 CenterY=76.4095 CenterZ=0 NormalX=0 NormalY=0 NormalZ=1 AngleXU=0 Radius=1
    g362: Circle CenterX=-10.9272 CenterY=72.4095 CenterZ=0 NormalX=0 NormalY=0 NormalZ=1 AngleXU=0 Radius=1
    g363: BSplineCurve PolesCount=3 KnotsCount=2 Degree=2 IsPeriodic=0
    g364: GeomPoint X=-6.92718 Y=76.4095 Z=0
    g365: GeomPoint X=-10.9272 Y=72.4095 Z=0
    g366: LineSegment StartX=-10.9272 StartY=72.4095 StartZ=0 EndX=-10.9272 EndY=-78.7794 EndZ=0
    g367: LineSegment StartX=-7.42095 StartY=-80.8542 StartZ=0 EndX=42.5666 EndY=-53.4075 EndZ=0
    g368: LineSegment StartX=46.0728 StartY=-47.4823 StartZ=0 EndX=46.0728 EndY=72.4095 EndZ=0
    g369: LineSegment StartX=42.0728 StartY=76.4095 StartZ=0 EndX=-6.92719 EndY=76.4095 EndZ=0
    g370: LineSegment StartX=232.072 StartY=136.221 StartZ=0 EndX=232.072 EndY=-117.815 EndZ=0
    g371: LineSegment StartX=132.072 StartY=136.221 StartZ=0 EndX=132.072 EndY=-121.309 EndZ=0
    g372: LineSegment StartX=245.072 StartY=136.221 StartZ=0 EndX=245.072 EndY=-116.499 EndZ=0
    g373: LineSegment StartX=119.072 StartY=136.221 StartZ=0 EndX=119.072 EndY=-116.228 EndZ=0
    g374: LineSegment StartX=-42.9272 StartY=136.221 StartZ=0 EndX=407.073 EndY=136.221 EndZ=0
    g375: LineSegment StartX=232.072 StartY=136.221 StartZ=0 EndX=220.072 EndY=136.221 EndZ=0
    g376: LineSegment StartX=232.072 StartY=136.221 StartZ=0 EndX=232.072 EndY=124.221 EndZ=0
    g377: LineSegment StartX=220.072 StartY=136.221 StartZ=0 EndX=220.072 EndY=124.221 EndZ=0
    g378: LineSegment StartX=220.072 StartY=136.221 StartZ=0 EndX=226.072 EndY=136.221 EndZ=0
    g379: LineSegment StartX=220.072 StartY=136.221 StartZ=0 EndX=220.072 EndY=130.221 EndZ=0
    g380: LineSegment StartX=220.072 StartY=124.221 StartZ=0 EndX=226.072 EndY=124.221 EndZ=0
    g381: LineSegment StartX=232.072 StartY=124.221 StartZ=0 EndX=232.072 EndY=127.221 EndZ=0
    g382: LineSegment StartX=232.072 StartY=136.221 StartZ=0 EndX=232.072 EndY=133.221 EndZ=0
    g383-g387: Circle x5 (B-spline internal-alignment scaffolding for g388; pole/knot coordinates omitted)
    g388: BSplineCurve PolesCount=5 KnotsCount=3 Degree=3 IsPeriodic=0
    g389: GeomPoint X=232.072 Y=133.221 Z=0
    g390: GeomPoint X=223.072 Y=130.221 Z=0
    g391: GeomPoint X=232.072 Y=127.221 Z=0
    g392: LineSegment StartX=189.124 StartY=124.221 StartZ=0 EndX=302.073 EndY=124.221 EndZ=0
    g393: LineSegment StartX=132.072 StartY=136.221 StartZ=0 EndX=132.072 EndY=124.221 EndZ=0
    g394: LineSegment StartX=132.072 StartY=136.221 StartZ=0 EndX=144.072 EndY=136.221 EndZ=0
    g395: LineSegment StartX=144.072 StartY=136.221 StartZ=0 EndX=144.072 EndY=124.221 EndZ=0
    g396: LineSegment StartX=144.072 StartY=136.221 StartZ=0 EndX=138.072 EndY=136.221 EndZ=0
    g397: LineSegment StartX=144.072 StartY=136.221 StartZ=0 EndX=144.072 EndY=130.221 EndZ=0
    g398: LineSegment StartX=132.072 StartY=136.221 StartZ=0 EndX=132.072 EndY=133.221 EndZ=0
    g399: LineSegment StartX=132.072 StartY=133.221 StartZ=0 EndX=132.072 EndY=127.221 EndZ=0
    g400-g404: Circle x5 (B-spline internal-alignment scaffolding for g405; pole/knot coordinates omitted)
    g405: BSplineCurve PolesCount=5 KnotsCount=3 Degree=3 IsPeriodic=0
    g406: GeomPoint X=132.072 Y=133.221 Z=0
    g407: GeomPoint X=141.072 Y=130.221 Z=0
    ... +2 more geometry lines
  constraints (696):
    c: Vertical(g0)
    c: Vertical(g1)
    c: Block(g1)
    c: Block(g0)
    c: Weight(g4) = 1
    c: Equal(g4,g5)
    c: Equal(g4,g6)
    c: InternalAlignment(g4,g7)
    c: InternalAlignment(g5,g7)
    c: InternalAlignment(g6,g7)
    c: InternalAlignment(g8,g7)
    c: InternalAlignment(g9,g7)
    c: Weight(g10) = 1
    c: Equal(g10,g11)
    c: Equal(g10,g12)
    c: InternalAlignment(g10,g13)
    c: InternalAlignment(g11,g13)
    c: InternalAlignment(g12,g13)
    c: InternalAlignment(g14,g13)
    c: InternalAlignment(g15,g13)
    c: Block(g13)
    c: Block(g7)
    c: Weight(g16) = 1
    c: Equal(g16,g17)
    c: Equal(g16,g18)
    c: InternalAlignment(g16,g19)
    c: InternalAlignment(g17,g19)
    c: InternalAlignment(g18,g19)
    c: InternalAlignment(g20,g19)
    c: InternalAlignment(g21,g19)
    c: Weight(g22) = 1
    c: Equal(g22,g23)
    c: Equal(g22,g24)
    c: InternalAlignment(g22,g25)
    c: InternalAlignment(g23,g25)
    c: InternalAlignment(g24,g25)
    c: InternalAlignment(g26,g25)
    c: InternalAlignment(g27,g25)
    c: Block(g25)
    c: Block(g19)
    c: Weight(g28) = 1
    c: Equal(g28,g29)
    c: Equal(g28,g30)
    c: InternalAlignment(g28,g31)
    c: InternalAlignment(g29,g31)
    c: InternalAlignment(g30,g31)
    c: InternalAlignment(g32,g31)
    c: InternalAlignment(g33,g31)
    c: Weight(g34) = 1
    c: Equal(g34,g35)
    c: Equal(g34,g36)
    c: InternalAlignment(g34,g37)
    c: InternalAlignment(g35,g37)
    c: InternalAlignment(g36,g37)
    c: InternalAlignment(g38,g37)
    c: InternalAlignment(g39,g37)
    c: Block(g31)
    c: Block(g37)
    c: Coincident(g40,g1)
    c: Coincident(g40,g0)
    c: Horizontal(g40)
    c: Distance(g40) = 450
    c: Weight(g41) = 1
    c: Equal(g41,g42)
    c: Equal(g41,g43)
    c: InternalAlignment(g41,g44)
    c: InternalAlignment(g42,g44)
    c: InternalAlignment(g43,g44)
    c: InternalAlignment(g45,g44)
    c: InternalAlignment(g46,g44)
    c: Block(g44)
    c: Weight(g47) = 1
    c: Equal(g47,g48)
    c: Equal(g47,g49)
    c: InternalAlignment(g47,g50)
    c: InternalAlignment(g48,g50)
    c: InternalAlignment(g49,g50)
    c: InternalAlignment(g51,g50)
    c: InternalAlignment(g52,g50)
    c: Block(g50)
    c: Weight(g53) = 1
    c: Equal(g53,g54)
    c: Equal(g53,g55)
    c: InternalAlignment(g53,g56)
    c: InternalAlignment(g54,g56)
    c: InternalAlignment(g55,g56)
    c: InternalAlignment(g57,g56)
    c: InternalAlignment(g58,g56)
    c: Block(g56)
    c: Weight(g59) = 1
    c: Equal(g59,g60)
    c: Equal(g59,g61)
    c: InternalAlignment(g59,g62)
    c: InternalAlignment(g60,g62)
    c: InternalAlignment(g61,g62)
    c: InternalAlignment(g63,g62)
    c: InternalAlignment(g64,g62)
    c: Block(g62)
    c: Weight(g65) = 1
    c: Equal(g65,g66)
    c: Equal(g65,g67)
    c: InternalAlignment(g65,g68)
    c: InternalAlignment(g66,g68)
    c: InternalAlignment(g67,g68)
    c: InternalAlignment(g69,g68)
    c: InternalAlignment(g70,g68)
    c: Weight(g71) = 1
    c: Equal(g71,g72)
    c: Equal(g71,g73)
    c: InternalAlignment(g71,g74)
    c: InternalAlignment(g72,g74)
    c: InternalAlignment(g73,g74)
    c: InternalAlignment(g75,g74)
    c: InternalAlignment(g76,g74)
    c: Block(g68)
    c: Block(g74)
    c: Coincident(g77,g68)
    c: Coincident(g77,g74)
    c: Vertical(g77)
    c: Coincident(g78,g68)
    c: Coincident(g78,g50)
    c: Coincident(g79,g50)
    c: Coincident(g79,g74)
    c: Weight(g80) = 1
    c: Equal(g80,g81)
    c: Equal(g80,g82)
    c: InternalAlignment(g80,g83)
    c: InternalAlignment(g81,g83)
    c: InternalAlignment(g82,g83)
    c: InternalAlignment(g84,g83)
    c: InternalAlignment(g85,g83)
    c: Weight(g86) = 1
    c: Equal(g86,g87)
    c: Equal(g86,g88)
    c: InternalAlignment(g86,g89)
    c: InternalAlignment(g87,g89)
    c: InternalAlignment(g88,g89)
    c: InternalAlignment(g90,g89)
    c: InternalAlignment(g91,g89)
    c: Block(g83)
    c: Block(g89)
    c: Coincident(g92,g83)
    c: Coincident(g92,g89)
    c: Vertical(g92)
    c: Coincident(g93,g83)
    c: Coincident(g93,g44)
    c: Coincident(g94,g44)
    c: Coincident(g94,g89)
    c: Weight(g95) = 1
    c: Equal(g95,g96)
    c: Equal(g95,g97)
    c: InternalAlignment(g95,g98)
    c: InternalAlignment(g96,g98)
    c: InternalAlignment(g97,g98)
    c: InternalAlignment(g99,g98)
    c: InternalAlignment(g100,g98)
    c: Weight(g101) = 1
    c: Equal(g101,g102)
    c: Equal(g101,g103)
    c: InternalAlignment(g101,g104)
    c: InternalAlignment(g102,g104)
    c: InternalAlignment(g103,g104)
    c: InternalAlignment(g105,g104)
    c: InternalAlignment(g106,g104)
    c: Block(g98)
    c: Block(g104)
    c: Coincident(g107,g98)
    c: Coincident(g107,g104)
    c: Vertical(g107)
    c: Coincident(g108,g104)
    c: Coincident(g108,g62)
    c: Coincident(g109,g62)
    c: Coincident(g109,g98)
    c: Weight(g110) = 1
    c: Equal(g110,g111)
    c: Equal(g110,g112)
    c: InternalAlignment(g110,g113)
    c: InternalAlignment(g111,g113)
    c: InternalAlignment(g112,g113)
    c: InternalAlignment(g114,g113)
    c: InternalAlignment(g115,g113)
    c: Weight(g116) = 1
    c: Equal(g116,g117)
    c: Equal(g116,g118)
    c: InternalAlignment(g116,g119)
    c: InternalAlignment(g117,g119)
    c: InternalAlignment(g118,g119)
    c: InternalAlignment(g120,g119)
    c: InternalAlignment(g121,g119)
    c: Block(g113)
    c: Block(g119)
    c: Coincident(g122,g113)
    c: Coincident(g122,g119)
    c: Vertical(g122)
    c: Coincident(g123,g119)
    c: Coincident(g123,g56)
    c: Coincident(g124,g56)
    c: Coincident(g124,g113)
    c: Weight(g125) = 1
    c: Equal(g125,g126)
    c: Equal(g125,g127)
    c: InternalAlignment(g125,g128)
    c: InternalAlignment(g126,g128)
    c: InternalAlignment(g127,g128)
    c: InternalAlignment(g129,g128)
    c: InternalAlignment(g130,g128)
    c: Weight(g131) = 1
    c: Equal(g131,g132)
    c: Equal(g131,g133)
    c: InternalAlignment(g131,g134)
    c: InternalAlignment(g132,g134)
    c: InternalAlignment(g133,g134)
    c: InternalAlignment(g135,g134)
    c: InternalAlignment(g136,g134)
    c: Weight(g137) = 1
    c: Equal(g137,g138)
    c: Equal(g137,g139)
    c: InternalAlignment(g137,g140)
    c: InternalAlignment(g138,g140)
    c: InternalAlignment(g139,g140)
    c: InternalAlignment(g141,g140)
    c: InternalAlignment(g142,g140)
    c: Weight(g143) = 1
    c: Equal(g143,g144)
    c: Equal(g143,g145)
    c: InternalAlignment(g143,g146)
    c: InternalAlignment(g144,g146)
    c: InternalAlignment(g145,g146)
    c: InternalAlignment(g147,g146)
    c: InternalAlignment(g148,g146)
    c: Block(g146)
    c: Block(g140)
    c: Block(g134)
    c: Block(g128)
    c: Coincident(g149,g25)
    c: Coincident(g149,g146)
    c: Coincident(g150,g146)
    c: Coincident(g150,g140)
    c: Horizontal(g150)
    c: Coincident(g151,g140)
    c: Coincident(g151,g25)
    c: Vertical(g151)
    c: Coincident(g152,g19)
    c: Coincident(g152,g134)
    c: Vertical(g152)
    c: Coincident(g153,g134)
    c: Coincident(g153,g128)
    c: Horizontal(g153)
    c: Coincident(g154,g128)
    c: Coincident(g154,g19)
    c: Weight(g155) = 1
    c: Equal(g155,g156)
    c: Equal(g155,g157)
    c: InternalAlignment(g155,g158)
    c: InternalAlignment(g156,g158)
    c: InternalAlignment(g157,g158)
    c: InternalAlignment(g159,g158)
    c: InternalAlignment(g160,g158)
    c: Weight(g161) = 1
    c: Equal(g161,g162)
    c: Equal(g161,g163)
    c: InternalAlignment(g161,g164)
    c: InternalAlignment(g162,g164)
    c: InternalAlignment(g163,g164)
    c: InternalAlignment(g165,g164)
    c: InternalAlignment(g166,g164)
    c: Weight(g167) = 1
    c: Equal(g167,g168)
    c: Equal(g167,g169)
    c: InternalAlignment(g167,g170)
    c: InternalAlignment(g168,g170)
    c: InternalAlignment(g169,g170)
    c: InternalAlignment(g171,g170)
    c: InternalAlignment(g172,g170)
    c: Weight(g173) = 1
    c: Equal(g173,g174)
    c: Equal(g173,g175)
    c: InternalAlignment(g173,g176)
    c: InternalAlignment(g174,g176)
    c: InternalAlignment(g175,g176)
    c: InternalAlignment(g177,g176)
    c: InternalAlignment(g178,g176)
    c: Block(g176)
    c: Block(g170)
    c: Block(g164)
    c: Block(g158)
    c: Coincident(g179,g170)
    c: Coincident(g179,g7)
    c: Vertical(g179)
    c: Coincident(g180,g13)
    c: Coincident(g180,g164)
    c: Vertical(g180)
    c: Coincident(g181,g158)
    c: Coincident(g181,g13)
    c: Coincident(g182,g7)
    c: Weight(g183) = 1
    c: Equal(g183,g184)
    c: Equal(g183,g185)
    c: InternalAlignment(g183,g186)
    c: InternalAlignment(g184,g186)
    c: InternalAlignment(g185,g186)
    c: InternalAlignment(g187,g186)
    c: InternalAlignment(g188,g186)
    c: Weight(g189) = 1
    c: Equal(g189,g190)
    c: Equal(g189,g191)
    c: InternalAlignment(g189,g192)
    c: InternalAlignment(g190,g192)
    c: InternalAlignment(g191,g192)
    c: InternalAlignment(g193,g192)
    c: InternalAlignment(g194,g192)
    c: Block(g192)
    c: Block(g186)
    c: Coincident(g195,g192)
    c: Coincident(g195,g31)
    c: Coincident(g196,g31)
    c: Coincident(g196,g186)
    c: Coincident(g197,g186)
    c: Coincident(g197,g192)
    c: Vertical(g197)
    c: Weight(g198) = 1
    c: Equal(g198,g199)
    c: Equal(g198,g200)
    c: InternalAlignment(g198,g201)
    c: InternalAlignment(g199,g201)
    c: InternalAlignment(g200,g201)
    c: InternalAlignment(g202,g201)
    c: InternalAlignment(g203,g201)
    c: Weight(g204) = 1
    c: Equal(g204,g205)
    c: Equal(g204,g206)
    c: InternalAlignment(g204,g207)
    c: InternalAlignment(g205,g207)
    c: InternalAlignment(g206,g207)
    c: InternalAlignment(g208,g207)
    c: InternalAlignment(g209,g207)
    c: Block(g207)
    c: Block(g201)
    c: Coincident(g210,g201)
    c: Coincident(g210,g37)
    c: Coincident(g211,g37)
    c: Coincident(g211,g207)
    c: Coincident(g212,g207)
    c: Coincident(g212,g201)
    c: Vertical(g212)
    c: Horizontal(g213)
    c: Block(g213)
    c: Vertical(g214)
    c: Block(g214)
    c: Block(g215)
    c: Weight(g216) = 1
    c: Equal(g216,g217)
    c: Equal(g216,g218)
    c: InternalAlignment(g216,g219)
    c: InternalAlignment(g217,g219)
    c: InternalAlignment(g218,g219)
    c: InternalAlignment(g220,g219)
    c: InternalAlignment(g221,g219)
    c: Weight(g222) = 1
    c: Equal(g222,g223)
    c: Equal(g222,g224)
    c: InternalAlignment(g222,g225)
    c: InternalAlignment(g223,g225)
    c: InternalAlignment(g224,g225)
    c: InternalAlignment(g226,g225)
    c: InternalAlignment(g227,g225)
    c: Weight(g228) = 1
    c: Equal(g228,g229)
    c: Equal(g228,g230)
    c: InternalAlignment(g228,g231)
    c: InternalAlignment(g229,g231)
    c: InternalAlignment(g230,g231)
    c: InternalAlignment(g232,g231)
    c: InternalAlignment(g233,g231)
    c: Weight(g234) = 1
    c: Equal(g234,g235)
    c: Equal(g234,g236)
    c: InternalAlignment(g234,g237)
    c: InternalAlignment(g235,g237)
    c: InternalAlignment(g236,g237)
    c: InternalAlignment(g238,g237)
    c: InternalAlignment(g239,g237)
    c: Block(g219)
    c: Block(g225)
    c: Block(g231)
    c: Block(g237)
    c: Coincident(g240,g225)
    c: Coincident(g240,g219)
    c: Horizontal(g240)
    c: Block(g182)
    c: Weight(g241) = 1
    c: Equal(g241,g242)
    c: Equal(g241,g243)
    c: InternalAlignment(g241,g244)
    c: InternalAlignment(g242,g244)
    c: InternalAlignment(g243,g244)
    c: InternalAlignment(g245,g244)
    c: InternalAlignment(g246,g244)
    c: Weight(g247) = 1
    c: Equal(g247,g248)
    c: Equal(g247,g249)
    c: InternalAlignment(g247,g250)
    c: InternalAlignment(g248,g250)
    c: InternalAlignment(g249,g250)
    c: InternalAlignment(g251,g250)
    c: InternalAlignment(g252,g250)
    c: Block(g244)
    c: Block(g250)
    c: Coincident(g253,g244)
    c: Coincident(g253,g250)
    c: Weight(g254) = 1
    c: Equal(g254,g255)
    c: Equal(g254,g256)
    c: InternalAlignment(g254,g257)
    c: InternalAlignment(g255,g257)
    c: InternalAlignment(g256,g257)
    c: InternalAlignment(g258,g257)
    c: InternalAlignment(g259,g257)
    c: Weight(g260) = 1
    c: Equal(g260,g261)
    c: Equal(g260,g262)
    c: InternalAlignment(g260,g263)
    c: InternalAlignment(g261,g263)
    c: InternalAlignment(g262,g263)
    c: InternalAlignment(g264,g263)
    c: InternalAlignment(g265,g263)
    c: Weight(g266) = 1
    c: Equal(g266,g267)
    c: Equal(g266,g268)
    c: InternalAlignment(g266,g269)
    c: InternalAlignment(g267,g269)
    c: InternalAlignment(g268,g269)
    c: InternalAlignment(g270,g269)
    c: InternalAlignment(g271,g269)
    c: Block(g269)
    c: Block(g263)
    c: Block(g257)
    c: Coincident(g272,g263)
    c: Coincident(g272,g257)
    c: Coincident(g273,g257)
    c: Coincident(g273,g269)
    c: Vertical(g273)
    c: Coincident(g274,g269)
    c: Coincident(g274,g263)
    c: Horizontal(g274)
    c: Weight(g275) = 1
    c: Equal(g275,g276)
    c: InternalAlignment(g275,g277)
    c: InternalAlignment(g276,g277)
    c: InternalAlignment(g278,g277)
    c: InternalAlignment(g279,g277)
    c: Weight(g280) = 1
    c: InternalAlignment(g281,g283)
    c: InternalAlignment(g282,g283)
    c: InternalAlignment(g284,g283)
    c: InternalAlignment(g285,g283)
    c: Weight(g286) = 1
    c: Equal(g286,g287)
    c: Equal(g286,g288)
    c: InternalAlignment(g286,g289)
    c: InternalAlignment(g287,g289)
    c: InternalAlignment(g288,g289)
    c: InternalAlignment(g290,g289)
    c: InternalAlignment(g291,g289)
    c: Equal(g292,g293)
    c: Equal(g292,g294)
    c: InternalAlignment(g292,g295)
    c: InternalAlignment(g293,g295)
    c: InternalAlignment(g294,g295)
    c: InternalAlignment(g296,g295)
    c: InternalAlignment(g297,g295)
    c: Block(g283)
    c: Block(g289)
    c: Block(g295)
    c: Block(g277)
    c: Coincident(g298,g277)
    c: Coincident(g298,g283)
    c: Horizontal(g298)
    c: Coincident(g299,g283)
    c: Coincident(g299,g289)
    c: Vertical(g299)
    c: Coincident(g300,g289)
    c: Coincident(g300,g295)
    c: Horizontal(g300)
    c: Coincident(g301,g295)
    c: Coincident(g301,g277)
    c: Weight(g302) = 1
    c: Equal(g302,g303)
    c: Equal(g302,g304)
    c: InternalAlignment(g302,g305)
    c: InternalAlignment(g303,g305)
    c: InternalAlignment(g304,g305)
    c: InternalAlignment(g306,g305)
    c: InternalAlignment(g307,g305)
    c: Weight(g308) = 1
    c: Equal(g308,g309)
    c: Equal(g308,g310)
    c: InternalAlignment(g308,g311)
    c: InternalAlignment(g309,g311)
    c: InternalAlignment(g310,g311)
    c: InternalAlignment(g312,g311)
    c: Weight(g314) = 1
    c: Equal(g314,g315)
    c: Equal(g314,g316)
    c: InternalAlignment(g314,g317)
    c: InternalAlignment(g315,g317)
    c: InternalAlignment(g316,g317)
    c: InternalAlignment(g318,g317)
    c: InternalAlignment(g319,g317)
    c: Block(g317)
    c: Block(g311)
    c: Block(g305)
    c: Coincident(g320,g317)
    c: Coincident(g320,g311)
    c: Horizontal(g320)
    c: Coincident(g321,g311)
    c: Coincident(g321,g305)
    c: Vertical(g321)
    c: Coincident(g322,g305)
    c: Coincident(g322,g317)
    c: InternalAlignment(g323,g324)
    c: InternalAlignment(g325,g324)
    c: InternalAlignment(g326,g324)
    c: Block(g324)
    c: Equal(g327,g328)
    c: Equal(g327,g329)
    c: InternalAlignment(g327,g330)
    c: InternalAlignment(g328,g330)
    c: InternalAlignment(g329,g330)
    c: InternalAlignment(g331,g330)
    c: InternalAlignment(g332,g330)
    c: Block(g330)
    c: Coincident(g333,g324)
    c: Horizontal(g333)
    c: Block(g333)
    c: Coincident(g334,g324)
    c: Coincident(g334,g250)
    c: Vertical(g334)
    c: Coincident(g335,g330)
    c: Coincident(g335,g244)
    c: Vertical(g335)
    c: Block(g336)
    c: Block(g2)
    c: Distance(g334) = 119.89
    c: Coincident(g337,g336)
    c: Coincident(g337,g2)
    c: Coincident(g338,g2)
    c: Coincident(g338,g336)
    c: Block(g3)
    c: Block(g339)
    c: Coincident(g340,g339)
    c: Coincident(g340,g3)
    c: Coincident(g341,g339)
    c: Coincident(g341,g3)
    c: Block(g341)
    c: Block(g340)
    c: Weight(g342) = 1
    c: Equal(g342,g343)
    c: Equal(g342,g344)
    c: InternalAlignment(g342,g345)
    c: InternalAlignment(g343,g345)
    c: InternalAlignment(g344,g345)
    c: InternalAlignment(g346,g345)
    c: InternalAlignment(g347,g345)
    c: Weight(g348) = 1
    c: Equal(g348,g349)
    c: Equal(g348,g350)
    c: InternalAlignment(g348,g351)
    c: InternalAlignment(g349,g351)
    c: InternalAlignment(g350,g351)
    c: InternalAlignment(g352,g351)
    c: InternalAlignment(g353,g351)
    c: Weight(g354) = 1
    c: Equal(g354,g355)
    c: Equal(g354,g356)
    c: InternalAlignment(g354,g357)
    c: InternalAlignment(g355,g357)
    c: InternalAlignment(g356,g357)
    c: InternalAlignment(g358,g357)
    c: InternalAlignment(g359,g357)
    c: Weight(g360) = 1
    c: Equal(g360,g361)
    c: Equal(g360,g362)
    c: InternalAlignment(g360,g363)
    c: InternalAlignment(g361,g363)
    c: InternalAlignment(g362,g363)
    c: InternalAlignment(g364,g363)
    c: InternalAlignment(g365,g363)
    c: Block(g363)
    c: Block(g357)
    c: Block(g351)
    c: Block(g345)
    c: Coincident(g366,g363)
    c: Coincident(g366,g345)
    c: Vertical(g366)
    c: Coincident(g367,g345)
    c: Coincident(g367,g351)
    c: Coincident(g368,g351)
    c: Coincident(g368,g357)
    c: Vertical(g368)
    c: Coincident(g369,g357)
    c: Coincident(g369,g363)
    c: Horizontal(g369)
    c: Vertical(g370)
    c: Vertical(g371)
    c: Vertical(g372)
    c: Vertical(g373)
    c: Coincident(g374,g0)
    c: Coincident(g374,g1)
    c: Horizontal(g374)
    c: Block(g374)
    c: Distance(g374) = 450
    c: Block(g372)
    c: Block(g370)
    c: Block(g371)
    c: Block(g373)
    c: Distance(g0) = 240
    c: Horizontal(g375)
    c: Distance(g375) = 12
    c: Coincident(g375,g370)
    c: Vertical(g376)
    c: Distance(g376) = 12
    c: Coincident(g376,g370)
    c: Coincident(g377,g375)
    c: Vertical(g377)
    c: Horizontal(g378)
    c: Vertical(g379)
    c: Distance(g379) = 6
    c: Coincident(g379,g375)
    c: Coincident(g378,g375)
    c: Block(g377)
    c: Coincident(g380,g377)
    c: Horizontal(g380)
    c: Distance(g380) = 6
    c: Vertical(g381)
    c: Distance(g381) = 3
    c: Vertical(g382)
    c: Distance(g382) = 3
    c: Coincident(g382,g370)
    c: Coincident(g376,g381)
    c: Coincident(g388,g382)
    c: Weight(g383) = 1
    c: Equal(g383,g384)
    c: Coincident(g384,g378)
    c: Equal(g383,g385)
    c: Coincident(g385,g379)
    c: Equal(g383,g386)
    c: Coincident(g386,g380)
    c: Equal(g383,g387)
    c: Coincident(g388,g381)
    c: InternalAlignment(g383-g387 -> g388) x5
    c: InternalAlignment(g389,g388)
    c: InternalAlignment(g390,g388)
    c: InternalAlignment(g391,g388)
    c: Coincident(g392,g164)
    c: Coincident(g392,g158)
    c: Horizontal(g392)
    c: Block(g388)
    c: Vertical(g393)
    c: Distance(g393) = 12
    c: Coincident(g393,g371)
    c: Horizontal(g394)
    c: Distance(g394) = 12
    c: Coincident(g394,g371)
    c: Coincident(g395,g394)
    c: Vertical(g395)
    c: Distance(g395) = 12
    c: Horizontal(g396)
    c: Distance(g396) = 6
    c: Coincident(g396,g394)
    c: Vertical(g397)
    c: Distance(g397) = 6
    c: Coincident(g397,g394)
    c: Vertical(g398)
    c: Distance(g398) = 3
    c: Coincident(g398,g371)
    c: Vertical(g399)
    c: Distance(g399) = 6
    c: Coincident(g399,g398)
    c: Coincident(g405,g398)
    c: Weight(g400) = 1
    c: Equal(g400,g401)
    c: Coincident(g401,g396)
    c: Equal(g400,g402)
    c: Coincident(g402,g397)
    c: Equal(g400,g403)
    c: Equal(g400,g404)
    c: Coincident(g405,g399)
    c: InternalAlignment(g400-g404 -> g405) x5
    c: InternalAlignment(g406,g405)
    c: InternalAlignment(g407,g405)
    c: InternalAlignment(g408,g405)
    c: Coincident(g409,g393)
    c: Coincident(g409,g170)
    c: Horizontal(g409)
    c: Block(g405)
FEATURE [Part::Extrusion] Extrude005
  Base = -> Sketch003
  Dir = (0,0,1)
  DirMode = 2
  FaceMakerClass = Part::FaceMakerBullseye
  LengthFwd = 24
  LengthRev = 0
  Solid = true
  Symmetric = false
